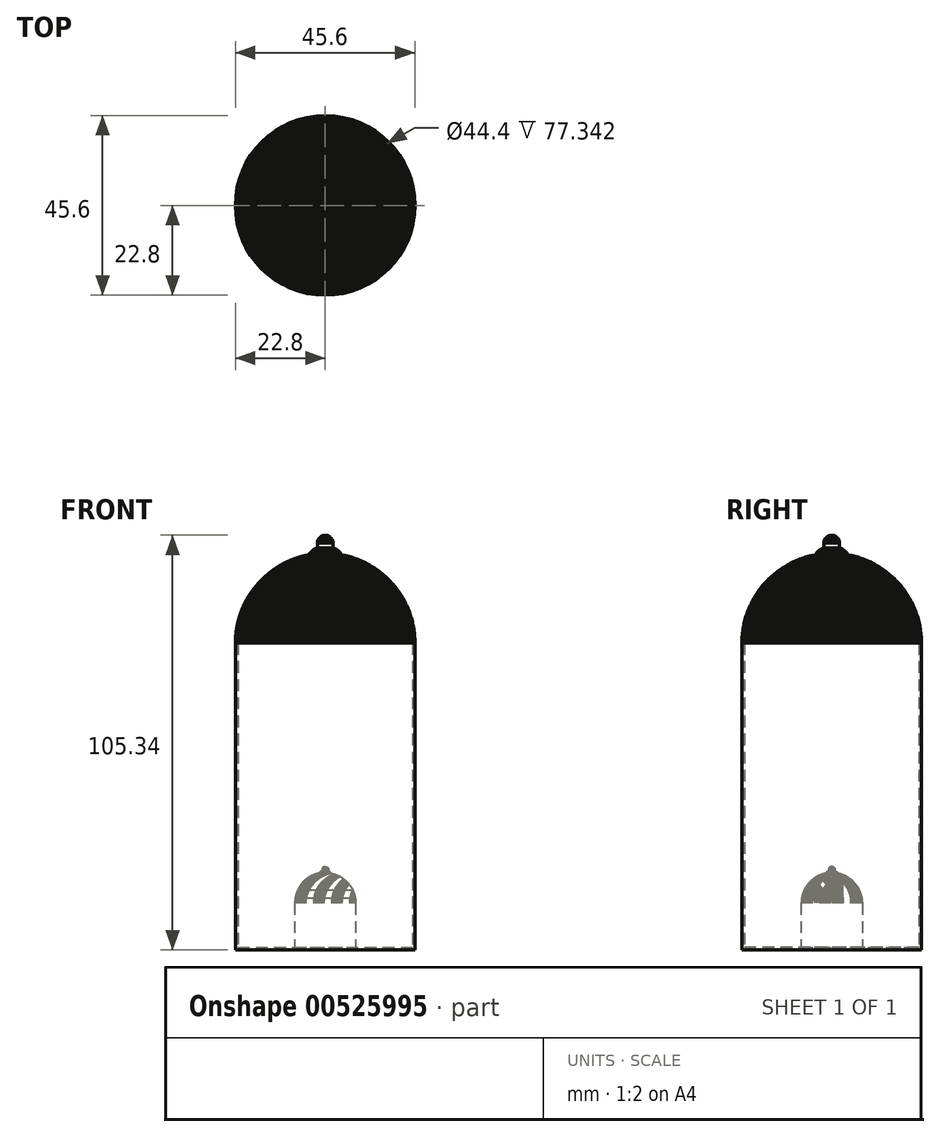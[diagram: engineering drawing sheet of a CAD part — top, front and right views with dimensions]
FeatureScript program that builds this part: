
annotation { "Feature Type Name" : "Feature", "Feature Type Description" : "" }
export const myFeature = defineFeature(function(context is Context, id is Id, definition is map)
    precondition{}
    {
        {
            var Q0;
            Q0=qCreatedBy(makeId("Front.planeOp"),FACE);
            var sketch = newSketch(context, id + "F0", { "sketchPlane" : qUnion([Q0])});
            skLineSegment(sketch, "E0", {"start": v(11.35, 52.66) * mm, "end": v(11.3, 52.66) * mm});
            skLineSegment(sketch, "E1", {"start": v(11.3, 52.66) * mm, "end": v(11.25, 52.66) * mm});
            skLineSegment(sketch, "E2", {"start": v(11.25, 52.66) * mm, "end": v(11.2, 52.66) * mm});
            skLineSegment(sketch, "E3", {"start": v(11.2, 52.66) * mm, "end": v(11.15, 52.65) * mm});
            skLineSegment(sketch, "E4", {"start": v(11.15, 52.65) * mm, "end": v(11.1, 52.64) * mm});
            skLineSegment(sketch, "E5", {"start": v(11.1, 52.64) * mm, "end": v(11.05, 52.63) * mm});
            skLineSegment(sketch, "E6", {"start": v(11.05, 52.63) * mm, "end": v(11, 52.62) * mm});
            skLineSegment(sketch, "E7", {"start": v(11, 52.62) * mm, "end": v(10.95, 52.61) * mm});
            skLineSegment(sketch, "E8", {"start": v(10.95, 52.61) * mm, "end": v(10.9, 52.6) * mm});
            skLineSegment(sketch, "E9", {"start": v(10.9, 52.6) * mm, "end": v(10.85, 52.59) * mm});
            skLineSegment(sketch, "E10", {"start": v(10.85, 52.59) * mm, "end": v(10.8, 52.58) * mm});
            skLineSegment(sketch, "E11", {"start": v(10.8, 52.58) * mm, "end": v(10.76, 52.56) * mm});
            skLineSegment(sketch, "E12", {"start": v(10.76, 52.56) * mm, "end": v(10.71, 52.54) * mm});
            skLineSegment(sketch, "E13", {"start": v(10.71, 52.54) * mm, "end": v(10.67, 52.53) * mm});
            skLineSegment(sketch, "E14", {"start": v(10.67, 52.53) * mm, "end": v(10.62, 52.5) * mm});
            skLineSegment(sketch, "E15", {"start": v(10.62, 52.5) * mm, "end": v(10.58, 52.49) * mm});
            skLineSegment(sketch, "E16", {"start": v(10.58, 52.49) * mm, "end": v(10.54, 52.47) * mm});
            skLineSegment(sketch, "E17", {"start": v(10.54, 52.47) * mm, "end": v(10.5, 52.45) * mm});
            skLineSegment(sketch, "E18", {"start": v(10.5, 52.45) * mm, "end": v(10.45, 52.42) * mm});
            skLineSegment(sketch, "E19", {"start": v(10.45, 52.42) * mm, "end": v(10.4, 52.4) * mm});
            skLineSegment(sketch, "E20", {"start": v(10.4, 52.4) * mm, "end": v(10.37, 52.38) * mm});
            skLineSegment(sketch, "E21", {"start": v(10.37, 52.38) * mm, "end": v(10.32, 52.35) * mm});
            skLineSegment(sketch, "E22", {"start": v(10.32, 52.35) * mm, "end": v(10.28, 52.32) * mm});
            skLineSegment(sketch, "E23", {"start": v(10.28, 52.32) * mm, "end": v(10.25, 52.3) * mm});
            skLineSegment(sketch, "E24", {"start": v(10.25, 52.3) * mm, "end": v(10.2, 52.27) * mm});
            skLineSegment(sketch, "E25", {"start": v(10.2, 52.27) * mm, "end": v(10.17, 52.24) * mm});
            skLineSegment(sketch, "E26", {"start": v(10.17, 52.24) * mm, "end": v(10.13, 52.2) * mm});
            skLineSegment(sketch, "E27", {"start": v(10.13, 52.2) * mm, "end": v(10.1, 52.18) * mm});
            skLineSegment(sketch, "E28", {"start": v(10.1, 52.18) * mm, "end": v(10.06, 52.15) * mm});
            skLineSegment(sketch, "E29", {"start": v(10.06, 52.15) * mm, "end": v(10.02, 52.11) * mm});
            skLineSegment(sketch, "E30", {"start": v(10.02, 52.11) * mm, "end": v(9.99, 52.08) * mm});
            skLineSegment(sketch, "E31", {"start": v(9.99, 52.08) * mm, "end": v(9.96, 52.05) * mm});
            skLineSegment(sketch, "E32", {"start": v(9.96, 52.05) * mm, "end": v(9.92, 52.01) * mm});
            skLineSegment(sketch, "E33", {"start": v(9.92, 52.01) * mm, "end": v(9.9, 51.97) * mm});
            skLineSegment(sketch, "E34", {"start": v(9.9, 51.97) * mm, "end": v(9.86, 51.94) * mm});
            skLineSegment(sketch, "E35", {"start": v(9.86, 51.94) * mm, "end": v(9.83, 51.9) * mm});
            skLineSegment(sketch, "E36", {"start": v(9.83, 51.9) * mm, "end": v(9.8, 51.86) * mm});
            skLineSegment(sketch, "E37", {"start": v(9.8, 51.86) * mm, "end": v(9.77, 51.82) * mm});
            skLineSegment(sketch, "E38", {"start": v(9.77, 51.82) * mm, "end": v(9.74, 51.78) * mm});
            skLineSegment(sketch, "E39", {"start": v(9.74, 51.78) * mm, "end": v(9.72, 51.74) * mm});
            skLineSegment(sketch, "E40", {"start": v(9.72, 51.74) * mm, "end": v(9.7, 51.7) * mm});
            skLineSegment(sketch, "E41", {"start": v(9.7, 51.7) * mm, "end": v(9.67, 51.66) * mm});
            skLineSegment(sketch, "E42", {"start": v(9.67, 51.66) * mm, "end": v(9.64, 51.62) * mm});
            skLineSegment(sketch, "E43", {"start": v(9.64, 51.62) * mm, "end": v(9.62, 51.58) * mm});
            skLineSegment(sketch, "E44", {"start": v(9.62, 51.58) * mm, "end": v(9.6, 51.53) * mm});
            skLineSegment(sketch, "E45", {"start": v(9.6, 51.53) * mm, "end": v(9.58, 51.49) * mm});
            skLineSegment(sketch, "E46", {"start": v(9.58, 51.49) * mm, "end": v(9.56, 51.45) * mm});
            skLineSegment(sketch, "E47", {"start": v(9.56, 51.45) * mm, "end": v(9.54, 51.4) * mm});
            skLineSegment(sketch, "E48", {"start": v(9.54, 51.4) * mm, "end": v(9.52, 51.35) * mm});
            skLineSegment(sketch, "E49", {"start": v(9.52, 51.35) * mm, "end": v(9.5, 51.3) * mm});
            skLineSegment(sketch, "E50", {"start": v(9.5, 51.3) * mm, "end": v(9.5, 51.26) * mm});
            skLineSegment(sketch, "E51", {"start": v(9.5, 51.26) * mm, "end": v(9.48, 51.21) * mm});
            skLineSegment(sketch, "E52", {"start": v(9.48, 51.21) * mm, "end": v(9.47, 51.17) * mm});
            skLineSegment(sketch, "E53", {"start": v(9.47, 51.17) * mm, "end": v(9.45, 51.12) * mm});
            skLineSegment(sketch, "E54", {"start": v(9.45, 51.12) * mm, "end": v(9.44, 51.07) * mm});
            skLineSegment(sketch, "E55", {"start": v(9.44, 51.07) * mm, "end": v(9.43, 51.02) * mm});
            skLineSegment(sketch, "E56", {"start": v(9.43, 51.02) * mm, "end": v(9.43, 50.97) * mm});
            skLineSegment(sketch, "E57", {"start": v(9.43, 50.97) * mm, "end": v(9.42, 50.92) * mm});
            skLineSegment(sketch, "E58", {"start": v(9.42, 50.92) * mm, "end": v(9.41, 50.87) * mm});
            skLineSegment(sketch, "E59", {"start": v(9.41, 50.87) * mm, "end": v(9.4, 50.82) * mm});
            skLineSegment(sketch, "E60", {"start": v(9.4, 50.82) * mm, "end": v(9.4, 50.77) * mm});
            skLineSegment(sketch, "E61", {"start": v(9.4, 50.77) * mm, "end": v(9.4, 50.72) * mm});
            skLineSegment(sketch, "E62", {"start": v(9.4, 50.72) * mm, "end": v(9.4, 50.67) * mm});
            skLineSegment(sketch, "E63", {"start": v(9.4, 50.67) * mm, "end": v(9.4, 50.65) * mm});
            skLineSegment(sketch, "E64", {"start": v(9.4, 50.65) * mm, "end": v(9.4, 50.63) * mm});
            skLineSegment(sketch, "E65", {"start": v(9.4, 50.63) * mm, "end": v(9.4, 50.61) * mm});
            skLineSegment(sketch, "E66", {"start": v(9.4, 50.61) * mm, "end": v(9.4, 50.6) * mm});
            skLineSegment(sketch, "E67", {"start": v(9.4, 50.6) * mm, "end": v(9.4, 50.58) * mm});
            skLineSegment(sketch, "E68", {"start": v(9.4, 50.58) * mm, "end": v(9.4, 50.56) * mm});
            skLineSegment(sketch, "E69", {"start": v(9.4, 50.56) * mm, "end": v(9.4, 50.54) * mm});
            skLineSegment(sketch, "E70", {"start": v(9.4, 50.54) * mm, "end": v(9.4, 50.52) * mm});
            skLineSegment(sketch, "E71", {"start": v(9.4, 50.52) * mm, "end": v(9.4, 50.5) * mm});
            skLineSegment(sketch, "E72", {"start": v(9.4, 50.5) * mm, "end": v(9.4, 50.49) * mm});
            skLineSegment(sketch, "E73", {"start": v(9.4, 50.49) * mm, "end": v(9.4, 50.47) * mm});
            skLineSegment(sketch, "E74", {"start": v(9.4, 50.47) * mm, "end": v(9.4, 50.45) * mm});
            skLineSegment(sketch, "E75", {"start": v(9.4, 50.45) * mm, "end": v(9.4, 50.43) * mm});
            skLineSegment(sketch, "E76", {"start": v(9.4, 50.43) * mm, "end": v(9.4, 50.41) * mm});
            skLineSegment(sketch, "E77", {"start": v(9.4, 50.41) * mm, "end": v(9.4, 50.4) * mm});
            skLineSegment(sketch, "E78", {"start": v(9.4, 50.4) * mm, "end": v(9.4, 50.37) * mm});
            skLineSegment(sketch, "E79", {"start": v(9.4, 50.37) * mm, "end": v(9.4, 50.36) * mm});
            skLineSegment(sketch, "E80", {"start": v(9.4, 50.36) * mm, "end": v(9.4, 50.34) * mm});
            skLineSegment(sketch, "E81", {"start": v(9.4, 50.34) * mm, "end": v(9.4, 50.32) * mm});
            skLineSegment(sketch, "E82", {"start": v(9.4, 50.32) * mm, "end": v(9.4, 50.3) * mm});
            skLineSegment(sketch, "E83", {"start": v(9.4, 50.3) * mm, "end": v(9.4, 50.28) * mm});
            skLineSegment(sketch, "E84", {"start": v(9.4, 50.28) * mm, "end": v(9.4, 50.26) * mm});
            skLineSegment(sketch, "E85", {"start": v(9.4, 50.26) * mm, "end": v(9.4, 50.25) * mm});
            skLineSegment(sketch, "E86", {"start": v(9.4, 50.25) * mm, "end": v(9.4, 50.23) * mm});
            skLineSegment(sketch, "E87", {"start": v(9.4, 50.23) * mm, "end": v(9.4, 50.2) * mm});
            skLineSegment(sketch, "E88", {"start": v(9.4, 50.2) * mm, "end": v(9.4, 50.2) * mm});
            skLineSegment(sketch, "E89", {"start": v(9.4, 50.2) * mm, "end": v(9.4, 50.17) * mm});
            skLineSegment(sketch, "E90", {"start": v(9.4, 50.17) * mm, "end": v(9.4, 50.15) * mm});
            skLineSegment(sketch, "E91", {"start": v(9.4, 50.15) * mm, "end": v(9.4, 50.14) * mm});
            skLineSegment(sketch, "E92", {"start": v(9.4, 50.14) * mm, "end": v(9.4, 50.12) * mm});
            skLineSegment(sketch, "E93", {"start": v(9.4, 50.12) * mm, "end": v(9.4, 50.1) * mm});
            skLineSegment(sketch, "E94", {"start": v(9.4, 50.1) * mm, "end": v(9.4, 50.08) * mm});
            skLineSegment(sketch, "E95", {"start": v(9.4, 50.08) * mm, "end": v(9.4, 50.06) * mm});
            skLineSegment(sketch, "E96", {"start": v(9.4, 50.06) * mm, "end": v(9.4, 50.04) * mm});
            skLineSegment(sketch, "E97", {"start": v(9.4, 50.04) * mm, "end": v(9.4, 50.03) * mm});
            skLineSegment(sketch, "E98", {"start": v(9.4, 50.03) * mm, "end": v(9.4, 50) * mm});
            skLineSegment(sketch, "E99", {"start": v(9.4, 50) * mm, "end": v(9.4, 49.99) * mm});
            skLineSegment(sketch, "E100", {"start": v(9.4, 49.99) * mm, "end": v(9.4, 49.97) * mm});
            skLineSegment(sketch, "E101", {"start": v(9.4, 49.97) * mm, "end": v(9.4, 49.95) * mm});
            skLineSegment(sketch, "E102", {"start": v(9.4, 49.95) * mm, "end": v(9.4, 49.93) * mm});
            skLineSegment(sketch, "E103", {"start": v(9.4, 49.93) * mm, "end": v(9.4, 49.92) * mm});
            skLineSegment(sketch, "E104", {"start": v(9.4, 49.92) * mm, "end": v(9.4, 49.9) * mm});
            skLineSegment(sketch, "E105", {"start": v(9.4, 49.9) * mm, "end": v(9.4, 49.88) * mm});
            skLineSegment(sketch, "E106", {"start": v(9.4, 49.88) * mm, "end": v(9.4, 49.86) * mm});
            skLineSegment(sketch, "E107", {"start": v(9.4, 49.86) * mm, "end": v(9.4, 49.84) * mm});
            skLineSegment(sketch, "E108", {"start": v(9.4, 49.84) * mm, "end": v(9.4, 49.82) * mm});
            skLineSegment(sketch, "E109", {"start": v(9.4, 49.82) * mm, "end": v(9.4, 49.8) * mm});
            skLineSegment(sketch, "E110", {"start": v(9.4, 49.8) * mm, "end": v(9.4, 49.79) * mm});
            skLineSegment(sketch, "E111", {"start": v(9.4, 49.79) * mm, "end": v(9.4, 49.77) * mm});
            skLineSegment(sketch, "E112", {"start": v(9.4, 49.77) * mm, "end": v(9.4, 49.75) * mm});
            skLineSegment(sketch, "E113", {"start": v(9.4, 49.75) * mm, "end": v(9.4, 49.73) * mm});
            skLineSegment(sketch, "E114", {"start": v(9.4, 49.73) * mm, "end": v(9.4, 49.71) * mm});
            skLineSegment(sketch, "E115", {"start": v(9.4, 49.71) * mm, "end": v(9.4, 49.7) * mm});
            skLineSegment(sketch, "E116", {"start": v(9.4, 49.7) * mm, "end": v(9.4, 49.68) * mm});
            skLineSegment(sketch, "E117", {"start": v(9.4, 49.68) * mm, "end": v(9.4, 49.66) * mm});
            skLineSegment(sketch, "E118", {"start": v(9.4, 49.66) * mm, "end": v(9.4, 49.64) * mm});
            skLineSegment(sketch, "E119", {"start": v(9.4, 49.64) * mm, "end": v(9.4, 49.62) * mm});
            skLineSegment(sketch, "E120", {"start": v(9.4, 49.62) * mm, "end": v(9.4, 49.6) * mm});
            skLineSegment(sketch, "E121", {"start": v(9.4, 49.6) * mm, "end": v(9.4, 49.58) * mm});
            skLineSegment(sketch, "E122", {"start": v(9.4, 49.58) * mm, "end": v(9.4, 49.57) * mm});
            skLineSegment(sketch, "E123", {"start": v(9.4, 49.57) * mm, "end": v(9.4, 49.55) * mm});
            skLineSegment(sketch, "E124", {"start": v(9.4, 49.55) * mm, "end": v(9.4, 49.53) * mm});
            skLineSegment(sketch, "E125", {"start": v(9.4, 49.53) * mm, "end": v(9.4, 49.51) * mm});
            skLineSegment(sketch, "E126", {"start": v(9.4, 49.51) * mm, "end": v(9.4, 49.5) * mm});
            skLineSegment(sketch, "E127", {"start": v(9.4, 49.5) * mm, "end": v(9.36, 49.47) * mm});
            skLineSegment(sketch, "E128", {"start": v(9.36, 49.47) * mm, "end": v(9.3, 49.46) * mm});
            skLineSegment(sketch, "E129", {"start": v(9.3, 49.46) * mm, "end": v(9.26, 49.44) * mm});
            skLineSegment(sketch, "E130", {"start": v(9.26, 49.44) * mm, "end": v(9.22, 49.42) * mm});
            skLineSegment(sketch, "E131", {"start": v(9.22, 49.42) * mm, "end": v(9.17, 49.4) * mm});
            skLineSegment(sketch, "E132", {"start": v(9.17, 49.4) * mm, "end": v(9.13, 49.38) * mm});
            skLineSegment(sketch, "E133", {"start": v(9.13, 49.38) * mm, "end": v(9.08, 49.36) * mm});
            skLineSegment(sketch, "E134", {"start": v(9.08, 49.36) * mm, "end": v(9.04, 49.34) * mm});
            skLineSegment(sketch, "E135", {"start": v(9.04, 49.34) * mm, "end": v(9, 49.32) * mm});
            skLineSegment(sketch, "E136", {"start": v(9, 49.32) * mm, "end": v(8.95, 49.3) * mm});
            skLineSegment(sketch, "E137", {"start": v(8.95, 49.3) * mm, "end": v(8.9, 49.28) * mm});
            skLineSegment(sketch, "E138", {"start": v(8.9, 49.28) * mm, "end": v(8.86, 49.25) * mm});
            skLineSegment(sketch, "E139", {"start": v(8.86, 49.25) * mm, "end": v(8.82, 49.23) * mm});
            skLineSegment(sketch, "E140", {"start": v(8.82, 49.23) * mm, "end": v(8.77, 49.2) * mm});
            skLineSegment(sketch, "E141", {"start": v(8.77, 49.2) * mm, "end": v(8.73, 49.19) * mm});
            skLineSegment(sketch, "E142", {"start": v(8.73, 49.19) * mm, "end": v(8.7, 49.16) * mm});
            skLineSegment(sketch, "E143", {"start": v(8.7, 49.16) * mm, "end": v(8.65, 49.14) * mm});
            skLineSegment(sketch, "E144", {"start": v(8.65, 49.14) * mm, "end": v(8.6, 49.11) * mm});
            skLineSegment(sketch, "E145", {"start": v(8.6, 49.11) * mm, "end": v(8.57, 49.1) * mm});
            skLineSegment(sketch, "E146", {"start": v(8.57, 49.1) * mm, "end": v(8.53, 49.07) * mm});
            skLineSegment(sketch, "E147", {"start": v(8.53, 49.07) * mm, "end": v(8.49, 49.04) * mm});
            skLineSegment(sketch, "E148", {"start": v(8.49, 49.04) * mm, "end": v(8.45, 49.01) * mm});
            skLineSegment(sketch, "E149", {"start": v(8.45, 49.01) * mm, "end": v(8.4, 48.99) * mm});
            skLineSegment(sketch, "E150", {"start": v(8.4, 48.99) * mm, "end": v(8.37, 48.96) * mm});
            skLineSegment(sketch, "E151", {"start": v(8.37, 48.96) * mm, "end": v(8.33, 48.94) * mm});
            skLineSegment(sketch, "E152", {"start": v(8.33, 48.94) * mm, "end": v(8.3, 48.91) * mm});
            skLineSegment(sketch, "E153", {"start": v(8.3, 48.91) * mm, "end": v(8.26, 48.88) * mm});
            skLineSegment(sketch, "E154", {"start": v(8.26, 48.88) * mm, "end": v(8.22, 48.86) * mm});
            skLineSegment(sketch, "E155", {"start": v(8.22, 48.86) * mm, "end": v(8.18, 48.83) * mm});
            skLineSegment(sketch, "E156", {"start": v(8.18, 48.83) * mm, "end": v(8.15, 48.8) * mm});
            skLineSegment(sketch, "E157", {"start": v(8.15, 48.8) * mm, "end": v(8.11, 48.77) * mm});
            skLineSegment(sketch, "E158", {"start": v(8.11, 48.77) * mm, "end": v(8.08, 48.74) * mm});
            skLineSegment(sketch, "E159", {"start": v(8.08, 48.74) * mm, "end": v(8.04, 48.71) * mm});
            skLineSegment(sketch, "E160", {"start": v(8.04, 48.71) * mm, "end": v(8, 48.69) * mm});
            skLineSegment(sketch, "E161", {"start": v(8, 48.69) * mm, "end": v(7.98, 48.66) * mm});
            skLineSegment(sketch, "E162", {"start": v(7.98, 48.66) * mm, "end": v(7.94, 48.63) * mm});
            skLineSegment(sketch, "E163", {"start": v(7.94, 48.63) * mm, "end": v(7.91, 48.6) * mm});
            skLineSegment(sketch, "E164", {"start": v(7.91, 48.6) * mm, "end": v(7.88, 48.57) * mm});
            skLineSegment(sketch, "E165", {"start": v(7.88, 48.57) * mm, "end": v(7.85, 48.53) * mm});
            skLineSegment(sketch, "E166", {"start": v(7.85, 48.53) * mm, "end": v(7.82, 48.5) * mm});
            skLineSegment(sketch, "E167", {"start": v(7.82, 48.5) * mm, "end": v(7.78, 48.47) * mm});
            skLineSegment(sketch, "E168", {"start": v(7.78, 48.47) * mm, "end": v(7.75, 48.44) * mm});
            skLineSegment(sketch, "E169", {"start": v(7.75, 48.44) * mm, "end": v(7.72, 48.4) * mm});
            skLineSegment(sketch, "E170", {"start": v(7.72, 48.4) * mm, "end": v(7.7, 48.38) * mm});
            skLineSegment(sketch, "E171", {"start": v(7.7, 48.38) * mm, "end": v(7.67, 48.35) * mm});
            skLineSegment(sketch, "E172", {"start": v(7.67, 48.35) * mm, "end": v(7.64, 48.31) * mm});
            skLineSegment(sketch, "E173", {"start": v(7.64, 48.31) * mm, "end": v(7.61, 48.28) * mm});
            skLineSegment(sketch, "E174", {"start": v(7.61, 48.28) * mm, "end": v(7.58, 48.25) * mm});
            skLineSegment(sketch, "E175", {"start": v(7.58, 48.25) * mm, "end": v(7.56, 48.21) * mm});
            skLineSegment(sketch, "E176", {"start": v(7.56, 48.21) * mm, "end": v(7.53, 48.18) * mm});
            skLineSegment(sketch, "E177", {"start": v(7.53, 48.18) * mm, "end": v(7.5, 48.15) * mm});
            skLineSegment(sketch, "E178", {"start": v(7.5, 48.15) * mm, "end": v(7.48, 48.11) * mm});
            skLineSegment(sketch, "E179", {"start": v(7.48, 48.11) * mm, "end": v(7.45, 48.08) * mm});
            skLineSegment(sketch, "E180", {"start": v(7.45, 48.08) * mm, "end": v(7.43, 48.04) * mm});
            skLineSegment(sketch, "E181", {"start": v(7.43, 48.04) * mm, "end": v(7.4, 48) * mm});
            skLineSegment(sketch, "E182", {"start": v(7.4, 48) * mm, "end": v(7.38, 47.97) * mm});
            skLineSegment(sketch, "E183", {"start": v(7.38, 47.97) * mm, "end": v(7.36, 47.94) * mm});
            skLineSegment(sketch, "E184", {"start": v(7.36, 47.94) * mm, "end": v(7.34, 47.9) * mm});
            skLineSegment(sketch, "E185", {"start": v(7.34, 47.9) * mm, "end": v(7.32, 47.87) * mm});
            skLineSegment(sketch, "E186", {"start": v(7.32, 47.87) * mm, "end": v(7.3, 47.83) * mm});
            skLineSegment(sketch, "E187", {"start": v(7.3, 47.83) * mm, "end": v(7.28, 47.8) * mm});
            skLineSegment(sketch, "E188", {"start": v(7.28, 47.8) * mm, "end": v(7.26, 47.76) * mm});
            skLineSegment(sketch, "E189", {"start": v(7.26, 47.76) * mm, "end": v(7.24, 47.72) * mm});
            skLineSegment(sketch, "E190", {"start": v(7.24, 47.72) * mm, "end": v(7.22, 47.69) * mm});
            skLineSegment(sketch, "E191", {"start": v(7.22, 47.69) * mm, "end": v(6.71, 47.59) * mm});
            skLineSegment(sketch, "E192", {"start": v(6.71, 47.59) * mm, "end": v(6.21, 47.48) * mm});
            skLineSegment(sketch, "E193", {"start": v(6.21, 47.48) * mm, "end": v(5.72, 47.36) * mm});
            skLineSegment(sketch, "E194", {"start": v(5.72, 47.36) * mm, "end": v(5.23, 47.23) * mm});
            skLineSegment(sketch, "E195", {"start": v(5.23, 47.23) * mm, "end": v(4.74, 47.08) * mm});
            skLineSegment(sketch, "E196", {"start": v(4.74, 47.08) * mm, "end": v(4.26, 46.93) * mm});
            skLineSegment(sketch, "E197", {"start": v(4.26, 46.93) * mm, "end": v(3.79, 46.77) * mm});
            skLineSegment(sketch, "E198", {"start": v(3.79, 46.77) * mm, "end": v(3.32, 46.6) * mm});
            skLineSegment(sketch, "E199", {"start": v(3.32, 46.6) * mm, "end": v(2.85, 46.42) * mm});
            skLineSegment(sketch, "E200", {"start": v(2.85, 46.42) * mm, "end": v(2.4, 46.23) * mm});
            skLineSegment(sketch, "E201", {"start": v(2.4, 46.23) * mm, "end": v(1.94, 46.03) * mm});
            skLineSegment(sketch, "E202", {"start": v(1.94, 46.03) * mm, "end": v(1.5, 45.82) * mm});
            skLineSegment(sketch, "E203", {"start": v(1.5, 45.82) * mm, "end": v(1.05, 45.6) * mm});
            skLineSegment(sketch, "E204", {"start": v(1.05, 45.6) * mm, "end": v(0.61, 45.37) * mm});
            skLineSegment(sketch, "E205", {"start": v(0.61, 45.37) * mm, "end": v(0.18, 45.13) * mm});
            skLineSegment(sketch, "E206", {"start": v(0.18, 45.13) * mm, "end": v(-0.25, 44.89) * mm});
            skLineSegment(sketch, "E207", {"start": v(-0.25, 44.89) * mm, "end": v(-0.67, 44.63) * mm});
            skLineSegment(sketch, "E208", {"start": v(-0.67, 44.63) * mm, "end": v(-1.08, 44.37) * mm});
            skLineSegment(sketch, "E209", {"start": v(-1.08, 44.37) * mm, "end": v(-1.48, 44.1) * mm});
            skLineSegment(sketch, "E210", {"start": v(-1.48, 44.1) * mm, "end": v(-1.88, 43.82) * mm});
            skLineSegment(sketch, "E211", {"start": v(-1.88, 43.82) * mm, "end": v(-2.28, 43.53) * mm});
            skLineSegment(sketch, "E212", {"start": v(-2.28, 43.53) * mm, "end": v(-2.67, 43.24) * mm});
            skLineSegment(sketch, "E213", {"start": v(-2.67, 43.24) * mm, "end": v(-3.04, 42.93) * mm});
            skLineSegment(sketch, "E214", {"start": v(-3.04, 42.93) * mm, "end": v(-3.42, 42.62) * mm});
            skLineSegment(sketch, "E215", {"start": v(-3.42, 42.62) * mm, "end": v(-3.78, 42.3) * mm});
            skLineSegment(sketch, "E216", {"start": v(-3.78, 42.3) * mm, "end": v(-4.14, 41.97) * mm});
            skLineSegment(sketch, "E217", {"start": v(-4.14, 41.97) * mm, "end": v(-4.5, 41.64) * mm});
            skLineSegment(sketch, "E218", {"start": v(-4.5, 41.64) * mm, "end": v(-4.84, 41.3) * mm});
            skLineSegment(sketch, "E219", {"start": v(-4.84, 41.3) * mm, "end": v(-5.18, 40.95) * mm});
            skLineSegment(sketch, "E220", {"start": v(-5.18, 40.95) * mm, "end": v(-5.5, 40.6) * mm});
            skLineSegment(sketch, "E221", {"start": v(-5.5, 40.6) * mm, "end": v(-5.83, 40.23) * mm});
            skLineSegment(sketch, "E222", {"start": v(-5.83, 40.23) * mm, "end": v(-6.14, 39.86) * mm});
            skLineSegment(sketch, "E223", {"start": v(-6.14, 39.86) * mm, "end": v(-6.45, 39.48) * mm});
            skLineSegment(sketch, "E224", {"start": v(-6.45, 39.48) * mm, "end": v(-6.74, 39.1) * mm});
            skLineSegment(sketch, "E225", {"start": v(-6.74, 39.1) * mm, "end": v(-7.03, 38.71) * mm});
            skLineSegment(sketch, "E226", {"start": v(-7.03, 38.71) * mm, "end": v(-7.31, 38.32) * mm});
            skLineSegment(sketch, "E227", {"start": v(-7.31, 38.32) * mm, "end": v(-7.59, 37.92) * mm});
            skLineSegment(sketch, "E228", {"start": v(-7.59, 37.92) * mm, "end": v(-7.85, 37.5) * mm});
            skLineSegment(sketch, "E229", {"start": v(-7.85, 37.5) * mm, "end": v(-8.1, 37.1) * mm});
            skLineSegment(sketch, "E230", {"start": v(-8.1, 37.1) * mm, "end": v(-8.36, 36.68) * mm});
            skLineSegment(sketch, "E231", {"start": v(-8.36, 36.68) * mm, "end": v(-8.6, 36.25) * mm});
            skLineSegment(sketch, "E232", {"start": v(-8.6, 36.25) * mm, "end": v(-8.82, 35.82) * mm});
            skLineSegment(sketch, "E233", {"start": v(-8.82, 35.82) * mm, "end": v(-9.05, 35.39) * mm});
            skLineSegment(sketch, "E234", {"start": v(-9.05, 35.39) * mm, "end": v(-9.26, 34.95) * mm});
            skLineSegment(sketch, "E235", {"start": v(-9.26, 34.95) * mm, "end": v(-9.46, 34.5) * mm});
            skLineSegment(sketch, "E236", {"start": v(-9.46, 34.5) * mm, "end": v(-9.65, 34.05) * mm});
            skLineSegment(sketch, "E237", {"start": v(-9.65, 34.05) * mm, "end": v(-9.84, 33.6) * mm});
            skLineSegment(sketch, "E238", {"start": v(-9.84, 33.6) * mm, "end": v(-10, 33.14) * mm});
            skLineSegment(sketch, "E239", {"start": v(-10, 33.14) * mm, "end": v(-10.17, 32.68) * mm});
            skLineSegment(sketch, "E240", {"start": v(-10.17, 32.68) * mm, "end": v(-10.33, 32.2) * mm});
            skLineSegment(sketch, "E241", {"start": v(-10.33, 32.2) * mm, "end": v(-10.47, 31.74) * mm});
            skLineSegment(sketch, "E242", {"start": v(-10.47, 31.74) * mm, "end": v(-10.6, 31.26) * mm});
            skLineSegment(sketch, "E243", {"start": v(-10.6, 31.26) * mm, "end": v(-10.73, 30.78) * mm});
            skLineSegment(sketch, "E244", {"start": v(-10.73, 30.78) * mm, "end": v(-10.85, 30.3) * mm});
            skLineSegment(sketch, "E245", {"start": v(-10.85, 30.3) * mm, "end": v(-10.95, 29.8) * mm});
            skLineSegment(sketch, "E246", {"start": v(-10.95, 29.8) * mm, "end": v(-11.04, 29.32) * mm});
            skLineSegment(sketch, "E247", {"start": v(-11.04, 29.32) * mm, "end": v(-11.13, 28.82) * mm});
            skLineSegment(sketch, "E248", {"start": v(-11.13, 28.82) * mm, "end": v(-11.2, 28.33) * mm});
            skLineSegment(sketch, "E249", {"start": v(-11.2, 28.33) * mm, "end": v(-11.26, 27.82) * mm});
            skLineSegment(sketch, "E250", {"start": v(-11.26, 27.82) * mm, "end": v(-11.3, 27.32) * mm});
            skLineSegment(sketch, "E251", {"start": v(-11.3, 27.32) * mm, "end": v(-11.35, 26.81) * mm});
            skLineSegment(sketch, "E252", {"start": v(-11.35, 26.81) * mm, "end": v(-11.38, 26.3) * mm});
            skLineSegment(sketch, "E253", {"start": v(-11.38, 26.3) * mm, "end": v(-11.4, 25.8) * mm});
            skLineSegment(sketch, "E254", {"start": v(-11.4, 25.8) * mm, "end": v(-11.4, 25.28) * mm});
            skLineSegment(sketch, "E255", {"start": v(-11.4, 25.28) * mm, "end": v(-11.4, 24.06) * mm});
            skLineSegment(sketch, "E256", {"start": v(-11.4, 24.06) * mm, "end": v(-11.4, 22.84) * mm});
            skLineSegment(sketch, "E257", {"start": v(-11.4, 22.84) * mm, "end": v(-11.4, 21.62) * mm});
            skLineSegment(sketch, "E258", {"start": v(-11.4, 21.62) * mm, "end": v(-11.4, 20.4) * mm});
            skLineSegment(sketch, "E259", {"start": v(-11.4, 20.4) * mm, "end": v(-11.4, 19.19) * mm});
            skLineSegment(sketch, "E260", {"start": v(-11.4, 19.19) * mm, "end": v(-11.4, 17.97) * mm});
            skLineSegment(sketch, "E261", {"start": v(-11.4, 17.97) * mm, "end": v(-11.4, 16.75) * mm});
            skLineSegment(sketch, "E262", {"start": v(-11.4, 16.75) * mm, "end": v(-11.4, 15.53) * mm});
            skLineSegment(sketch, "E263", {"start": v(-11.4, 15.53) * mm, "end": v(-11.4, 14.32) * mm});
            skLineSegment(sketch, "E264", {"start": v(-11.4, 14.32) * mm, "end": v(-11.4, 13.1) * mm});
            skLineSegment(sketch, "E265", {"start": v(-11.4, 13.1) * mm, "end": v(-11.4, 11.88) * mm});
            skLineSegment(sketch, "E266", {"start": v(-11.4, 11.88) * mm, "end": v(-11.4, 10.66) * mm});
            skLineSegment(sketch, "E267", {"start": v(-11.4, 10.66) * mm, "end": v(-11.4, 9.44) * mm});
            skLineSegment(sketch, "E268", {"start": v(-11.4, 9.44) * mm, "end": v(-11.4, 8.23) * mm});
            skLineSegment(sketch, "E269", {"start": v(-11.4, 8.23) * mm, "end": v(-11.4, 7) * mm});
            skLineSegment(sketch, "E270", {"start": v(-11.4, 7) * mm, "end": v(-11.4, 5.8) * mm});
            skLineSegment(sketch, "E271", {"start": v(-11.4, 5.8) * mm, "end": v(-11.4, 4.57) * mm});
            skLineSegment(sketch, "E272", {"start": v(-11.4, 4.57) * mm, "end": v(-11.4, 3.36) * mm});
            skLineSegment(sketch, "E273", {"start": v(-11.4, 3.36) * mm, "end": v(-11.4, 2.14) * mm});
            skLineSegment(sketch, "E274", {"start": v(-11.4, 2.14) * mm, "end": v(-11.4, 0.92) * mm});
            skLineSegment(sketch, "E275", {"start": v(-11.4, 0.92) * mm, "end": v(-11.4, -0.3) * mm});
            skLineSegment(sketch, "E276", {"start": v(-11.4, -0.3) * mm, "end": v(-11.4, -1.52) * mm});
            skLineSegment(sketch, "E277", {"start": v(-11.4, -1.52) * mm, "end": v(-11.4, -2.73) * mm});
            skLineSegment(sketch, "E278", {"start": v(-11.4, -2.73) * mm, "end": v(-11.4, -3.95) * mm});
            skLineSegment(sketch, "E279", {"start": v(-11.4, -3.95) * mm, "end": v(-11.4, -5.17) * mm});
            skLineSegment(sketch, "E280", {"start": v(-11.4, -5.17) * mm, "end": v(-11.4, -6.39) * mm});
            skLineSegment(sketch, "E281", {"start": v(-11.4, -6.39) * mm, "end": v(-11.4, -7.6) * mm});
            skLineSegment(sketch, "E282", {"start": v(-11.4, -7.6) * mm, "end": v(-11.4, -8.82) * mm});
            skLineSegment(sketch, "E283", {"start": v(-11.4, -8.82) * mm, "end": v(-11.4, -10.04) * mm});
            skLineSegment(sketch, "E284", {"start": v(-11.4, -10.04) * mm, "end": v(-11.4, -11.26) * mm});
            skLineSegment(sketch, "E285", {"start": v(-11.4, -11.26) * mm, "end": v(-11.4, -12.48) * mm});
            skLineSegment(sketch, "E286", {"start": v(-11.4, -12.48) * mm, "end": v(-11.4, -13.7) * mm});
            skLineSegment(sketch, "E287", {"start": v(-11.4, -13.7) * mm, "end": v(-11.4, -14.91) * mm});
            skLineSegment(sketch, "E288", {"start": v(-11.4, -14.91) * mm, "end": v(-11.4, -16.13) * mm});
            skLineSegment(sketch, "E289", {"start": v(-11.4, -16.13) * mm, "end": v(-11.4, -17.35) * mm});
            skLineSegment(sketch, "E290", {"start": v(-11.4, -17.35) * mm, "end": v(-11.4, -18.57) * mm});
            skLineSegment(sketch, "E291", {"start": v(-11.4, -18.57) * mm, "end": v(-11.4, -19.78) * mm});
            skLineSegment(sketch, "E292", {"start": v(-11.4, -19.78) * mm, "end": v(-11.4, -21) * mm});
            skLineSegment(sketch, "E293", {"start": v(-11.4, -21) * mm, "end": v(-11.4, -22.22) * mm});
            skLineSegment(sketch, "E294", {"start": v(-11.4, -22.22) * mm, "end": v(-11.4, -23.44) * mm});
            skLineSegment(sketch, "E295", {"start": v(-11.4, -23.44) * mm, "end": v(-11.4, -24.66) * mm});
            skLineSegment(sketch, "E296", {"start": v(-11.4, -24.66) * mm, "end": v(-11.4, -25.87) * mm});
            skLineSegment(sketch, "E297", {"start": v(-11.4, -25.87) * mm, "end": v(-11.4, -27.1) * mm});
            skLineSegment(sketch, "E298", {"start": v(-11.4, -27.1) * mm, "end": v(-11.4, -28.3) * mm});
            skLineSegment(sketch, "E299", {"start": v(-11.4, -28.3) * mm, "end": v(-11.4, -29.53) * mm});
            skLineSegment(sketch, "E300", {"start": v(-11.4, -29.53) * mm, "end": v(-11.4, -30.74) * mm});
            skLineSegment(sketch, "E301", {"start": v(-11.4, -30.74) * mm, "end": v(-11.4, -31.96) * mm});
            skLineSegment(sketch, "E302", {"start": v(-11.4, -31.96) * mm, "end": v(-11.4, -33.18) * mm});
            skLineSegment(sketch, "E303", {"start": v(-11.4, -33.18) * mm, "end": v(-11.4, -34.4) * mm});
            skLineSegment(sketch, "E304", {"start": v(-11.4, -34.4) * mm, "end": v(-11.4, -35.62) * mm});
            skLineSegment(sketch, "E305", {"start": v(-11.4, -35.62) * mm, "end": v(-11.4, -36.83) * mm});
            skLineSegment(sketch, "E306", {"start": v(-11.4, -36.83) * mm, "end": v(-11.4, -38.05) * mm});
            skLineSegment(sketch, "E307", {"start": v(-11.4, -38.05) * mm, "end": v(-11.4, -39.27) * mm});
            skLineSegment(sketch, "E308", {"start": v(-11.4, -39.27) * mm, "end": v(-11.4, -40.49) * mm});
            skLineSegment(sketch, "E309", {"start": v(-11.4, -40.49) * mm, "end": v(-11.4, -41.7) * mm});
            skLineSegment(sketch, "E310", {"start": v(-11.4, -41.7) * mm, "end": v(-11.4, -42.92) * mm});
            skLineSegment(sketch, "E311", {"start": v(-11.4, -42.92) * mm, "end": v(-11.4, -44.14) * mm});
            skLineSegment(sketch, "E312", {"start": v(-11.4, -44.14) * mm, "end": v(-11.4, -45.36) * mm});
            skLineSegment(sketch, "E313", {"start": v(-11.4, -45.36) * mm, "end": v(-11.4, -46.58) * mm});
            skLineSegment(sketch, "E314", {"start": v(-11.4, -46.58) * mm, "end": v(-11.4, -47.8) * mm});
            skLineSegment(sketch, "E315", {"start": v(-11.4, -47.8) * mm, "end": v(-11.4, -49.01) * mm});
            skLineSegment(sketch, "E316", {"start": v(-11.4, -49.01) * mm, "end": v(-11.4, -50.23) * mm});
            skLineSegment(sketch, "E317", {"start": v(-11.4, -50.23) * mm, "end": v(-11.4, -51.45) * mm});
            skLineSegment(sketch, "E318", {"start": v(-11.4, -51.45) * mm, "end": v(-11.4, -52.67) * mm});
            skLineSegment(sketch, "E319", {"start": v(-11.4, -52.67) * mm, "end": v(-11.16, -52.67) * mm});
            skLineSegment(sketch, "E320", {"start": v(-11.16, -52.67) * mm, "end": v(-10.91, -52.67) * mm});
            skLineSegment(sketch, "E321", {"start": v(-10.91, -52.67) * mm, "end": v(-10.67, -52.67) * mm});
            skLineSegment(sketch, "E322", {"start": v(-10.67, -52.67) * mm, "end": v(-10.42, -52.67) * mm});
            skLineSegment(sketch, "E323", {"start": v(-10.42, -52.67) * mm, "end": v(-10.18, -52.67) * mm});
            skLineSegment(sketch, "E324", {"start": v(-10.18, -52.67) * mm, "end": v(-9.93, -52.67) * mm});
            skLineSegment(sketch, "E325", {"start": v(-9.93, -52.67) * mm, "end": v(-9.69, -52.67) * mm});
            skLineSegment(sketch, "E326", {"start": v(-9.69, -52.67) * mm, "end": v(-9.44, -52.67) * mm});
            skLineSegment(sketch, "E327", {"start": v(-9.44, -52.67) * mm, "end": v(-9.2, -52.67) * mm});
            skLineSegment(sketch, "E328", {"start": v(-9.2, -52.67) * mm, "end": v(-8.95, -52.67) * mm});
            skLineSegment(sketch, "E329", {"start": v(-8.95, -52.67) * mm, "end": v(-8.71, -52.67) * mm});
            skLineSegment(sketch, "E330", {"start": v(-8.71, -52.67) * mm, "end": v(-8.47, -52.67) * mm});
            skLineSegment(sketch, "E331", {"start": v(-8.47, -52.67) * mm, "end": v(-8.22, -52.67) * mm});
            skLineSegment(sketch, "E332", {"start": v(-8.22, -52.67) * mm, "end": v(-7.98, -52.67) * mm});
            skLineSegment(sketch, "E333", {"start": v(-7.98, -52.67) * mm, "end": v(-7.73, -52.67) * mm});
            skLineSegment(sketch, "E334", {"start": v(-7.73, -52.67) * mm, "end": v(-7.49, -52.67) * mm});
            skLineSegment(sketch, "E335", {"start": v(-7.49, -52.67) * mm, "end": v(-7.24, -52.67) * mm});
            skLineSegment(sketch, "E336", {"start": v(-7.24, -52.67) * mm, "end": v(-7, -52.67) * mm});
            skLineSegment(sketch, "E337", {"start": v(-7, -52.67) * mm, "end": v(-6.75, -52.67) * mm});
            skLineSegment(sketch, "E338", {"start": v(-6.75, -52.67) * mm, "end": v(-6.5, -52.67) * mm});
            skLineSegment(sketch, "E339", {"start": v(-6.5, -52.67) * mm, "end": v(-6.26, -52.67) * mm});
            skLineSegment(sketch, "E340", {"start": v(-6.26, -52.67) * mm, "end": v(-6.02, -52.67) * mm});
            skLineSegment(sketch, "E341", {"start": v(-6.02, -52.67) * mm, "end": v(-5.78, -52.67) * mm});
            skLineSegment(sketch, "E342", {"start": v(-5.78, -52.67) * mm, "end": v(-5.53, -52.67) * mm});
            skLineSegment(sketch, "E343", {"start": v(-5.53, -52.67) * mm, "end": v(-5.29, -52.67) * mm});
            skLineSegment(sketch, "E344", {"start": v(-5.29, -52.67) * mm, "end": v(-5.04, -52.67) * mm});
            skLineSegment(sketch, "E345", {"start": v(-5.04, -52.67) * mm, "end": v(-4.8, -52.67) * mm});
            skLineSegment(sketch, "E346", {"start": v(-4.8, -52.67) * mm, "end": v(-4.55, -52.67) * mm});
            skLineSegment(sketch, "E347", {"start": v(-4.55, -52.67) * mm, "end": v(-4.3, -52.67) * mm});
            skLineSegment(sketch, "E348", {"start": v(-4.3, -52.67) * mm, "end": v(-4.06, -52.67) * mm});
            skLineSegment(sketch, "E349", {"start": v(-4.06, -52.67) * mm, "end": v(-3.82, -52.67) * mm});
            skLineSegment(sketch, "E350", {"start": v(-3.82, -52.67) * mm, "end": v(-3.57, -52.67) * mm});
            skLineSegment(sketch, "E351", {"start": v(-3.57, -52.67) * mm, "end": v(-3.33, -52.67) * mm});
            skLineSegment(sketch, "E352", {"start": v(-3.33, -52.67) * mm, "end": v(-3.09, -52.67) * mm});
            skLineSegment(sketch, "E353", {"start": v(-3.09, -52.67) * mm, "end": v(-2.84, -52.67) * mm});
            skLineSegment(sketch, "E354", {"start": v(-2.84, -52.67) * mm, "end": v(-2.6, -52.67) * mm});
            skLineSegment(sketch, "E355", {"start": v(-2.6, -52.67) * mm, "end": v(-2.35, -52.67) * mm});
            skLineSegment(sketch, "E356", {"start": v(-2.35, -52.67) * mm, "end": v(-2.1, -52.67) * mm});
            skLineSegment(sketch, "E357", {"start": v(-2.1, -52.67) * mm, "end": v(-1.86, -52.67) * mm});
            skLineSegment(sketch, "E358", {"start": v(-1.86, -52.67) * mm, "end": v(-1.62, -52.67) * mm});
            skLineSegment(sketch, "E359", {"start": v(-1.62, -52.67) * mm, "end": v(-1.37, -52.67) * mm});
            skLineSegment(sketch, "E360", {"start": v(-1.37, -52.67) * mm, "end": v(-1.13, -52.67) * mm});
            skLineSegment(sketch, "E361", {"start": v(-1.13, -52.67) * mm, "end": v(-0.88, -52.67) * mm});
            skLineSegment(sketch, "E362", {"start": v(-0.88, -52.67) * mm, "end": v(-0.64, -52.67) * mm});
            skLineSegment(sketch, "E363", {"start": v(-0.64, -52.67) * mm, "end": v(-0.4, -52.67) * mm});
            skLineSegment(sketch, "E364", {"start": v(-0.4, -52.67) * mm, "end": v(-0.15, -52.67) * mm});
            skLineSegment(sketch, "E365", {"start": v(-0.15, -52.67) * mm, "end": v(0.1, -52.67) * mm});
            skLineSegment(sketch, "E366", {"start": v(0.1, -52.67) * mm, "end": v(0.34, -52.67) * mm});
            skLineSegment(sketch, "E367", {"start": v(0.34, -52.67) * mm, "end": v(0.58, -52.67) * mm});
            skLineSegment(sketch, "E368", {"start": v(0.58, -52.67) * mm, "end": v(0.83, -52.67) * mm});
            skLineSegment(sketch, "E369", {"start": v(0.83, -52.67) * mm, "end": v(1.07, -52.67) * mm});
            skLineSegment(sketch, "E370", {"start": v(1.07, -52.67) * mm, "end": v(1.32, -52.67) * mm});
            skLineSegment(sketch, "E371", {"start": v(1.32, -52.67) * mm, "end": v(1.56, -52.67) * mm});
            skLineSegment(sketch, "E372", {"start": v(1.56, -52.67) * mm, "end": v(1.8, -52.67) * mm});
            skLineSegment(sketch, "E373", {"start": v(1.8, -52.67) * mm, "end": v(2.05, -52.67) * mm});
            skLineSegment(sketch, "E374", {"start": v(2.05, -52.67) * mm, "end": v(2.3, -52.67) * mm});
            skLineSegment(sketch, "E375", {"start": v(2.3, -52.67) * mm, "end": v(2.54, -52.67) * mm});
            skLineSegment(sketch, "E376", {"start": v(2.54, -52.67) * mm, "end": v(2.78, -52.67) * mm});
            skLineSegment(sketch, "E377", {"start": v(2.78, -52.67) * mm, "end": v(3.03, -52.67) * mm});
            skLineSegment(sketch, "E378", {"start": v(3.03, -52.67) * mm, "end": v(3.27, -52.67) * mm});
            skLineSegment(sketch, "E379", {"start": v(3.27, -52.67) * mm, "end": v(3.52, -52.67) * mm});
            skLineSegment(sketch, "E380", {"start": v(3.52, -52.67) * mm, "end": v(3.76, -52.67) * mm});
            skLineSegment(sketch, "E381", {"start": v(3.76, -52.67) * mm, "end": v(4, -52.67) * mm});
            skLineSegment(sketch, "E382", {"start": v(4, -52.67) * mm, "end": v(4.25, -52.67) * mm});
            skLineSegment(sketch, "E383", {"start": v(4.25, -52.67) * mm, "end": v(4.36, -52.67) * mm});
            skLineSegment(sketch, "E384", {"start": v(4.36, -52.67) * mm, "end": v(4.48, -52.67) * mm});
            skLineSegment(sketch, "E385", {"start": v(4.48, -52.67) * mm, "end": v(4.59, -52.67) * mm});
            skLineSegment(sketch, "E386", {"start": v(4.59, -52.67) * mm, "end": v(4.7, -52.67) * mm});
            skLineSegment(sketch, "E387", {"start": v(4.7, -52.67) * mm, "end": v(4.81, -52.67) * mm});
            skLineSegment(sketch, "E388", {"start": v(4.81, -52.67) * mm, "end": v(4.92, -52.67) * mm});
            skLineSegment(sketch, "E389", {"start": v(4.92, -52.67) * mm, "end": v(5.03, -52.67) * mm});
            skLineSegment(sketch, "E390", {"start": v(5.03, -52.67) * mm, "end": v(5.15, -52.67) * mm});
            skLineSegment(sketch, "E391", {"start": v(5.15, -52.67) * mm, "end": v(5.26, -52.67) * mm});
            skLineSegment(sketch, "E392", {"start": v(5.26, -52.67) * mm, "end": v(5.37, -52.67) * mm});
            skLineSegment(sketch, "E393", {"start": v(5.37, -52.67) * mm, "end": v(5.48, -52.67) * mm});
            skLineSegment(sketch, "E394", {"start": v(5.48, -52.67) * mm, "end": v(5.6, -52.67) * mm});
            skLineSegment(sketch, "E395", {"start": v(5.6, -52.67) * mm, "end": v(5.7, -52.67) * mm});
            skLineSegment(sketch, "E396", {"start": v(5.7, -52.67) * mm, "end": v(5.82, -52.67) * mm});
            skLineSegment(sketch, "E397", {"start": v(5.82, -52.67) * mm, "end": v(5.93, -52.67) * mm});
            skLineSegment(sketch, "E398", {"start": v(5.93, -52.67) * mm, "end": v(6.04, -52.67) * mm});
            skLineSegment(sketch, "E399", {"start": v(6.04, -52.67) * mm, "end": v(6.15, -52.67) * mm});
            skLineSegment(sketch, "E400", {"start": v(6.15, -52.67) * mm, "end": v(6.26, -52.67) * mm});
            skLineSegment(sketch, "E401", {"start": v(6.26, -52.67) * mm, "end": v(6.37, -52.67) * mm});
            skLineSegment(sketch, "E402", {"start": v(6.37, -52.67) * mm, "end": v(6.49, -52.67) * mm});
            skLineSegment(sketch, "E403", {"start": v(6.49, -52.67) * mm, "end": v(6.6, -52.67) * mm});
            skLineSegment(sketch, "E404", {"start": v(6.6, -52.67) * mm, "end": v(6.7, -52.67) * mm});
            skLineSegment(sketch, "E405", {"start": v(6.7, -52.67) * mm, "end": v(6.82, -52.67) * mm});
            skLineSegment(sketch, "E406", {"start": v(6.82, -52.67) * mm, "end": v(6.93, -52.67) * mm});
            skLineSegment(sketch, "E407", {"start": v(6.93, -52.67) * mm, "end": v(7.04, -52.67) * mm});
            skLineSegment(sketch, "E408", {"start": v(7.04, -52.67) * mm, "end": v(7.16, -52.67) * mm});
            skLineSegment(sketch, "E409", {"start": v(7.16, -52.67) * mm, "end": v(7.27, -52.67) * mm});
            skLineSegment(sketch, "E410", {"start": v(7.27, -52.67) * mm, "end": v(7.38, -52.67) * mm});
            skLineSegment(sketch, "E411", {"start": v(7.38, -52.67) * mm, "end": v(7.5, -52.67) * mm});
            skLineSegment(sketch, "E412", {"start": v(7.5, -52.67) * mm, "end": v(7.6, -52.67) * mm});
            skLineSegment(sketch, "E413", {"start": v(7.6, -52.67) * mm, "end": v(7.71, -52.67) * mm});
            skLineSegment(sketch, "E414", {"start": v(7.71, -52.67) * mm, "end": v(7.83, -52.67) * mm});
            skLineSegment(sketch, "E415", {"start": v(7.83, -52.67) * mm, "end": v(7.94, -52.67) * mm});
            skLineSegment(sketch, "E416", {"start": v(7.94, -52.67) * mm, "end": v(8.05, -52.67) * mm});
            skLineSegment(sketch, "E417", {"start": v(8.05, -52.67) * mm, "end": v(8.16, -52.67) * mm});
            skLineSegment(sketch, "E418", {"start": v(8.16, -52.67) * mm, "end": v(8.27, -52.67) * mm});
            skLineSegment(sketch, "E419", {"start": v(8.27, -52.67) * mm, "end": v(8.39, -52.67) * mm});
            skLineSegment(sketch, "E420", {"start": v(8.39, -52.67) * mm, "end": v(8.5, -52.67) * mm});
            skLineSegment(sketch, "E421", {"start": v(8.5, -52.67) * mm, "end": v(8.6, -52.67) * mm});
            skLineSegment(sketch, "E422", {"start": v(8.6, -52.67) * mm, "end": v(8.72, -52.67) * mm});
            skLineSegment(sketch, "E423", {"start": v(8.72, -52.67) * mm, "end": v(8.83, -52.67) * mm});
            skLineSegment(sketch, "E424", {"start": v(8.83, -52.67) * mm, "end": v(8.94, -52.67) * mm});
            skLineSegment(sketch, "E425", {"start": v(8.94, -52.67) * mm, "end": v(9.05, -52.67) * mm});
            skLineSegment(sketch, "E426", {"start": v(9.05, -52.67) * mm, "end": v(9.17, -52.67) * mm});
            skLineSegment(sketch, "E427", {"start": v(9.17, -52.67) * mm, "end": v(9.28, -52.67) * mm});
            skLineSegment(sketch, "E428", {"start": v(9.28, -52.67) * mm, "end": v(9.39, -52.67) * mm});
            skLineSegment(sketch, "E429", {"start": v(9.39, -52.67) * mm, "end": v(9.5, -52.67) * mm});
            skLineSegment(sketch, "E430", {"start": v(9.5, -52.67) * mm, "end": v(9.61, -52.67) * mm});
            skLineSegment(sketch, "E431", {"start": v(9.61, -52.67) * mm, "end": v(9.73, -52.67) * mm});
            skLineSegment(sketch, "E432", {"start": v(9.73, -52.67) * mm, "end": v(9.84, -52.67) * mm});
            skLineSegment(sketch, "E433", {"start": v(9.84, -52.67) * mm, "end": v(9.95, -52.67) * mm});
            skLineSegment(sketch, "E434", {"start": v(9.95, -52.67) * mm, "end": v(10.06, -52.67) * mm});
            skLineSegment(sketch, "E435", {"start": v(10.06, -52.67) * mm, "end": v(10.17, -52.67) * mm});
            skLineSegment(sketch, "E436", {"start": v(10.17, -52.67) * mm, "end": v(10.28, -52.67) * mm});
            skLineSegment(sketch, "E437", {"start": v(10.28, -52.67) * mm, "end": v(10.4, -52.67) * mm});
            skLineSegment(sketch, "E438", {"start": v(10.4, -52.67) * mm, "end": v(10.5, -52.67) * mm});
            skLineSegment(sketch, "E439", {"start": v(10.5, -52.67) * mm, "end": v(10.62, -52.67) * mm});
            skLineSegment(sketch, "E440", {"start": v(10.62, -52.67) * mm, "end": v(10.73, -52.67) * mm});
            skLineSegment(sketch, "E441", {"start": v(10.73, -52.67) * mm, "end": v(10.84, -52.67) * mm});
            skLineSegment(sketch, "E442", {"start": v(10.84, -52.67) * mm, "end": v(10.95, -52.67) * mm});
            skLineSegment(sketch, "E443", {"start": v(10.95, -52.67) * mm, "end": v(11.07, -52.67) * mm});
            skLineSegment(sketch, "E444", {"start": v(11.07, -52.67) * mm, "end": v(11.18, -52.67) * mm});
            skLineSegment(sketch, "E445", {"start": v(11.18, -52.67) * mm, "end": v(11.29, -52.67) * mm});
            skLineSegment(sketch, "E446", {"start": v(11.29, -52.67) * mm, "end": v(11.4, -52.67) * mm});
            skLineSegment(sketch, "E447", {"start": v(11.4, -52.67) * mm, "end": v(11.4, -52.34) * mm});
            skLineSegment(sketch, "E448", {"start": v(11.4, -52.34) * mm, "end": v(11.4, -52) * mm});
            skLineSegment(sketch, "E449", {"start": v(11.4, -52) * mm, "end": v(11.4, -51.67) * mm});
            skLineSegment(sketch, "E450", {"start": v(11.4, -51.67) * mm, "end": v(11.4, -51.34) * mm});
            skLineSegment(sketch, "E451", {"start": v(11.4, -51.34) * mm, "end": v(11.4, -51.01) * mm});
            skLineSegment(sketch, "E452", {"start": v(11.4, -51.01) * mm, "end": v(11.4, -50.68) * mm});
            skLineSegment(sketch, "E453", {"start": v(11.4, -50.68) * mm, "end": v(11.4, -50.35) * mm});
            skLineSegment(sketch, "E454", {"start": v(11.4, -50.35) * mm, "end": v(11.4, -50.02) * mm});
            skLineSegment(sketch, "E455", {"start": v(11.4, -50.02) * mm, "end": v(11.4, -49.7) * mm});
            skLineSegment(sketch, "E456", {"start": v(11.4, -49.7) * mm, "end": v(11.4, -49.36) * mm});
            skLineSegment(sketch, "E457", {"start": v(11.4, -49.36) * mm, "end": v(11.4, -49.03) * mm});
            skLineSegment(sketch, "E458", {"start": v(11.4, -49.03) * mm, "end": v(11.4, -48.7) * mm});
            skLineSegment(sketch, "E459", {"start": v(11.4, -48.7) * mm, "end": v(11.4, -48.37) * mm});
            skLineSegment(sketch, "E460", {"start": v(11.4, -48.37) * mm, "end": v(11.4, -48.04) * mm});
            skLineSegment(sketch, "E461", {"start": v(11.4, -48.04) * mm, "end": v(11.4, -47.71) * mm});
            skLineSegment(sketch, "E462", {"start": v(11.4, -47.71) * mm, "end": v(11.4, -47.38) * mm});
            skLineSegment(sketch, "E463", {"start": v(11.4, -47.38) * mm, "end": v(11.4, -47.05) * mm});
            skLineSegment(sketch, "E464", {"start": v(11.4, -47.05) * mm, "end": v(11.4, -46.72) * mm});
            skLineSegment(sketch, "E465", {"start": v(11.4, -46.72) * mm, "end": v(11.4, -46.4) * mm});
            skLineSegment(sketch, "E466", {"start": v(11.4, -46.4) * mm, "end": v(11.4, -46.06) * mm});
            skLineSegment(sketch, "E467", {"start": v(11.4, -46.06) * mm, "end": v(11.4, -45.73) * mm});
            skLineSegment(sketch, "E468", {"start": v(11.4, -45.73) * mm, "end": v(11.4, -45.4) * mm});
            skLineSegment(sketch, "E469", {"start": v(11.4, -45.4) * mm, "end": v(11.4, -45.07) * mm});
            skLineSegment(sketch, "E470", {"start": v(11.4, -45.07) * mm, "end": v(11.4, -44.74) * mm});
            skLineSegment(sketch, "E471", {"start": v(11.4, -44.74) * mm, "end": v(11.4, -44.4) * mm});
            skLineSegment(sketch, "E472", {"start": v(11.4, -44.4) * mm, "end": v(11.4, -44.08) * mm});
            skLineSegment(sketch, "E473", {"start": v(11.4, -44.08) * mm, "end": v(11.4, -43.75) * mm});
            skLineSegment(sketch, "E474", {"start": v(11.4, -43.75) * mm, "end": v(11.4, -43.42) * mm});
            skLineSegment(sketch, "E475", {"start": v(11.4, -43.42) * mm, "end": v(11.4, -43.09) * mm});
            skLineSegment(sketch, "E476", {"start": v(11.4, -43.09) * mm, "end": v(11.4, -42.76) * mm});
            skLineSegment(sketch, "E477", {"start": v(11.4, -42.76) * mm, "end": v(11.4, -42.43) * mm});
            skLineSegment(sketch, "E478", {"start": v(11.4, -42.43) * mm, "end": v(11.4, -42.1) * mm});
            skLineSegment(sketch, "E479", {"start": v(11.4, -42.1) * mm, "end": v(11.4, -41.77) * mm});
            skLineSegment(sketch, "E480", {"start": v(11.4, -41.77) * mm, "end": v(11.4, -41.44) * mm});
            skLineSegment(sketch, "E481", {"start": v(11.4, -41.44) * mm, "end": v(11.4, -41.1) * mm});
            skLineSegment(sketch, "E482", {"start": v(11.4, -41.1) * mm, "end": v(11.4, -40.78) * mm});
            skLineSegment(sketch, "E483", {"start": v(11.4, -40.78) * mm, "end": v(11.4, -40.45) * mm});
            skLineSegment(sketch, "E484", {"start": v(11.4, -40.45) * mm, "end": v(11.4, -40.12) * mm});
            skLineSegment(sketch, "E485", {"start": v(11.4, -40.12) * mm, "end": v(11.4, -39.79) * mm});
            skLineSegment(sketch, "E486", {"start": v(11.4, -39.79) * mm, "end": v(11.4, -39.46) * mm});
            skLineSegment(sketch, "E487", {"start": v(11.4, -39.46) * mm, "end": v(11.4, -39.13) * mm});
            skLineSegment(sketch, "E488", {"start": v(11.4, -39.13) * mm, "end": v(11.4, -38.8) * mm});
            skLineSegment(sketch, "E489", {"start": v(11.4, -38.8) * mm, "end": v(11.4, -38.47) * mm});
            skLineSegment(sketch, "E490", {"start": v(11.4, -38.47) * mm, "end": v(11.4, -38.14) * mm});
            skLineSegment(sketch, "E491", {"start": v(11.4, -38.14) * mm, "end": v(11.4, -37.8) * mm});
            skLineSegment(sketch, "E492", {"start": v(11.4, -37.8) * mm, "end": v(11.4, -37.47) * mm});
            skLineSegment(sketch, "E493", {"start": v(11.4, -37.47) * mm, "end": v(11.4, -37.14) * mm});
            skLineSegment(sketch, "E494", {"start": v(11.4, -37.14) * mm, "end": v(11.4, -36.81) * mm});
            skLineSegment(sketch, "E495", {"start": v(11.4, -36.81) * mm, "end": v(11.4, -36.48) * mm});
            skLineSegment(sketch, "E496", {"start": v(11.4, -36.48) * mm, "end": v(11.4, -36.15) * mm});
            skLineSegment(sketch, "E497", {"start": v(11.4, -36.15) * mm, "end": v(11.4, -35.82) * mm});
            skLineSegment(sketch, "E498", {"start": v(11.4, -35.82) * mm, "end": v(11.4, -35.5) * mm});
            skLineSegment(sketch, "E499", {"start": v(11.4, -35.5) * mm, "end": v(11.4, -35.16) * mm});
            skLineSegment(sketch, "E500", {"start": v(11.4, -35.16) * mm, "end": v(11.4, -34.83) * mm});
            skLineSegment(sketch, "E501", {"start": v(11.4, -34.83) * mm, "end": v(11.4, -34.5) * mm});
            skLineSegment(sketch, "E502", {"start": v(11.4, -34.5) * mm, "end": v(11.4, -34.17) * mm});
            skLineSegment(sketch, "E503", {"start": v(11.4, -34.17) * mm, "end": v(11.4, -33.84) * mm});
            skLineSegment(sketch, "E504", {"start": v(11.4, -33.84) * mm, "end": v(11.4, -33.51) * mm});
            skLineSegment(sketch, "E505", {"start": v(11.4, -33.51) * mm, "end": v(11.4, -33.18) * mm});
            skLineSegment(sketch, "E506", {"start": v(11.4, -33.18) * mm, "end": v(11.4, -32.85) * mm});
            skLineSegment(sketch, "E507", {"start": v(11.4, -32.85) * mm, "end": v(11.4, -32.52) * mm});
            skLineSegment(sketch, "E508", {"start": v(11.4, -32.52) * mm, "end": v(11.4, -32.2) * mm});
            skLineSegment(sketch, "E509", {"start": v(11.4, -32.2) * mm, "end": v(11.4, -31.86) * mm});
            skLineSegment(sketch, "E510", {"start": v(11.4, -31.86) * mm, "end": v(11.4, -31.53) * mm});
            skLineSegment(sketch, "E511", {"start": v(11.4, -31.53) * mm, "end": v(11.38, -31.53) * mm});
            skLineSegment(sketch, "E512", {"start": v(11.38, -31.53) * mm, "end": v(11.36, -31.53) * mm});
            skLineSegment(sketch, "E513", {"start": v(11.36, -31.53) * mm, "end": v(11.33, -31.53) * mm});
            skLineSegment(sketch, "E514", {"start": v(11.33, -31.53) * mm, "end": v(11.31, -31.53) * mm});
            skLineSegment(sketch, "E515", {"start": v(11.31, -31.53) * mm, "end": v(11.3, -31.54) * mm});
            skLineSegment(sketch, "E516", {"start": v(11.3, -31.54) * mm, "end": v(11.27, -31.54) * mm});
            skLineSegment(sketch, "E517", {"start": v(11.27, -31.54) * mm, "end": v(11.25, -31.54) * mm});
            skLineSegment(sketch, "E518", {"start": v(11.25, -31.54) * mm, "end": v(11.23, -31.55) * mm});
            skLineSegment(sketch, "E519", {"start": v(11.23, -31.55) * mm, "end": v(11.2, -31.55) * mm});
            skLineSegment(sketch, "E520", {"start": v(11.2, -31.55) * mm, "end": v(11.18, -31.56) * mm});
            skLineSegment(sketch, "E521", {"start": v(11.18, -31.56) * mm, "end": v(11.16, -31.56) * mm});
            skLineSegment(sketch, "E522", {"start": v(11.16, -31.56) * mm, "end": v(11.14, -31.57) * mm});
            skLineSegment(sketch, "E523", {"start": v(11.14, -31.57) * mm, "end": v(11.12, -31.58) * mm});
            skLineSegment(sketch, "E524", {"start": v(11.12, -31.58) * mm, "end": v(11.1, -31.58) * mm});
            skLineSegment(sketch, "E525", {"start": v(11.1, -31.58) * mm, "end": v(11.08, -31.6) * mm});
            skLineSegment(sketch, "E526", {"start": v(11.08, -31.6) * mm, "end": v(11.06, -31.6) * mm});
            skLineSegment(sketch, "E527", {"start": v(11.06, -31.6) * mm, "end": v(11.05, -31.6) * mm});
            skLineSegment(sketch, "E528", {"start": v(11.05, -31.6) * mm, "end": v(11.03, -31.62) * mm});
            skLineSegment(sketch, "E529", {"start": v(11.03, -31.62) * mm, "end": v(11, -31.62) * mm});
            skLineSegment(sketch, "E530", {"start": v(11, -31.62) * mm, "end": v(10.99, -31.63) * mm});
            skLineSegment(sketch, "E531", {"start": v(10.99, -31.63) * mm, "end": v(10.97, -31.64) * mm});
            skLineSegment(sketch, "E532", {"start": v(10.97, -31.64) * mm, "end": v(10.95, -31.65) * mm});
            skLineSegment(sketch, "E533", {"start": v(10.95, -31.65) * mm, "end": v(10.94, -31.67) * mm});
            skLineSegment(sketch, "E534", {"start": v(10.94, -31.67) * mm, "end": v(10.92, -31.68) * mm});
            skLineSegment(sketch, "E535", {"start": v(10.92, -31.68) * mm, "end": v(10.9, -31.69) * mm});
            skLineSegment(sketch, "E536", {"start": v(10.9, -31.69) * mm, "end": v(10.88, -31.7) * mm});
            skLineSegment(sketch, "E537", {"start": v(10.88, -31.7) * mm, "end": v(10.87, -31.71) * mm});
            skLineSegment(sketch, "E538", {"start": v(10.87, -31.71) * mm, "end": v(10.85, -31.73) * mm});
            skLineSegment(sketch, "E539", {"start": v(10.85, -31.73) * mm, "end": v(10.84, -31.74) * mm});
            skLineSegment(sketch, "E540", {"start": v(10.84, -31.74) * mm, "end": v(10.82, -31.75) * mm});
            skLineSegment(sketch, "E541", {"start": v(10.82, -31.75) * mm, "end": v(10.8, -31.77) * mm});
            skLineSegment(sketch, "E542", {"start": v(10.8, -31.77) * mm, "end": v(10.8, -31.78) * mm});
            skLineSegment(sketch, "E543", {"start": v(10.8, -31.78) * mm, "end": v(10.78, -31.8) * mm});
            skLineSegment(sketch, "E544", {"start": v(10.78, -31.8) * mm, "end": v(10.76, -31.81) * mm});
            skLineSegment(sketch, "E545", {"start": v(10.76, -31.81) * mm, "end": v(10.75, -31.83) * mm});
            skLineSegment(sketch, "E546", {"start": v(10.75, -31.83) * mm, "end": v(10.74, -31.84) * mm});
            skLineSegment(sketch, "E547", {"start": v(10.74, -31.84) * mm, "end": v(10.72, -31.86) * mm});
            skLineSegment(sketch, "E548", {"start": v(10.72, -31.86) * mm, "end": v(10.71, -31.88) * mm});
            skLineSegment(sketch, "E549", {"start": v(10.71, -31.88) * mm, "end": v(10.7, -31.9) * mm});
            skLineSegment(sketch, "E550", {"start": v(10.7, -31.9) * mm, "end": v(10.69, -31.91) * mm});
            skLineSegment(sketch, "E551", {"start": v(10.69, -31.91) * mm, "end": v(10.67, -31.93) * mm});
            skLineSegment(sketch, "E552", {"start": v(10.67, -31.93) * mm, "end": v(10.66, -31.95) * mm});
            skLineSegment(sketch, "E553", {"start": v(10.66, -31.95) * mm, "end": v(10.65, -31.96) * mm});
            skLineSegment(sketch, "E554", {"start": v(10.65, -31.96) * mm, "end": v(10.64, -31.98) * mm});
            skLineSegment(sketch, "E555", {"start": v(10.64, -31.98) * mm, "end": v(10.63, -32) * mm});
            skLineSegment(sketch, "E556", {"start": v(10.63, -32) * mm, "end": v(10.62, -32.02) * mm});
            skLineSegment(sketch, "E557", {"start": v(10.62, -32.02) * mm, "end": v(10.62, -32.04) * mm});
            skLineSegment(sketch, "E558", {"start": v(10.62, -32.04) * mm, "end": v(10.6, -32.06) * mm});
            skLineSegment(sketch, "E559", {"start": v(10.6, -32.06) * mm, "end": v(10.6, -32.08) * mm});
            skLineSegment(sketch, "E560", {"start": v(10.6, -32.08) * mm, "end": v(10.6, -32.1) * mm});
            skLineSegment(sketch, "E561", {"start": v(10.6, -32.1) * mm, "end": v(10.58, -32.12) * mm});
            skLineSegment(sketch, "E562", {"start": v(10.58, -32.12) * mm, "end": v(10.58, -32.14) * mm});
            skLineSegment(sketch, "E563", {"start": v(10.58, -32.14) * mm, "end": v(10.57, -32.16) * mm});
            skLineSegment(sketch, "E564", {"start": v(10.57, -32.16) * mm, "end": v(10.57, -32.18) * mm});
            skLineSegment(sketch, "E565", {"start": v(10.57, -32.18) * mm, "end": v(10.56, -32.2) * mm});
            skLineSegment(sketch, "E566", {"start": v(10.56, -32.2) * mm, "end": v(10.56, -32.22) * mm});
            skLineSegment(sketch, "E567", {"start": v(10.56, -32.22) * mm, "end": v(10.55, -32.24) * mm});
            skLineSegment(sketch, "E568", {"start": v(10.55, -32.24) * mm, "end": v(10.55, -32.26) * mm});
            skLineSegment(sketch, "E569", {"start": v(10.55, -32.26) * mm, "end": v(10.55, -32.28) * mm});
            skLineSegment(sketch, "E570", {"start": v(10.55, -32.28) * mm, "end": v(10.54, -32.3) * mm});
            skLineSegment(sketch, "E571", {"start": v(10.54, -32.3) * mm, "end": v(10.54, -32.33) * mm});
            skLineSegment(sketch, "E572", {"start": v(10.54, -32.33) * mm, "end": v(10.54, -32.35) * mm});
            skLineSegment(sketch, "E573", {"start": v(10.54, -32.35) * mm, "end": v(10.54, -32.37) * mm});
            skLineSegment(sketch, "E574", {"start": v(10.54, -32.37) * mm, "end": v(10.54, -32.4) * mm});
            skLineSegment(sketch, "E575", {"start": v(10.54, -32.4) * mm, "end": v(10.54, -32.4) * mm});
            skLineSegment(sketch, "E576", {"start": v(10.54, -32.4) * mm, "end": v(10.54, -32.41) * mm});
            skLineSegment(sketch, "E577", {"start": v(10.54, -32.41) * mm, "end": v(10.54, -32.42) * mm});
            skLineSegment(sketch, "E578", {"start": v(10.54, -32.42) * mm, "end": v(10.54, -32.42) * mm});
            skLineSegment(sketch, "E579", {"start": v(10.54, -32.42) * mm, "end": v(10.54, -32.43) * mm});
            skLineSegment(sketch, "E580", {"start": v(10.54, -32.43) * mm, "end": v(10.54, -32.43) * mm});
            skLineSegment(sketch, "E581", {"start": v(10.54, -32.43) * mm, "end": v(10.54, -32.44) * mm});
            skLineSegment(sketch, "E582", {"start": v(10.54, -32.44) * mm, "end": v(10.54, -32.44) * mm});
            skLineSegment(sketch, "E583", {"start": v(10.54, -32.44) * mm, "end": v(10.54, -32.45) * mm});
            skLineSegment(sketch, "E584", {"start": v(10.54, -32.45) * mm, "end": v(10.54, -32.45) * mm});
            skLineSegment(sketch, "E585", {"start": v(10.54, -32.45) * mm, "end": v(10.54, -32.46) * mm});
            skLineSegment(sketch, "E586", {"start": v(10.54, -32.46) * mm, "end": v(10.54, -32.46) * mm});
            skLineSegment(sketch, "E587", {"start": v(10.54, -32.46) * mm, "end": v(10.54, -32.47) * mm});
            skLineSegment(sketch, "E588", {"start": v(10.54, -32.47) * mm, "end": v(10.54, -32.47) * mm});
            skLineSegment(sketch, "E589", {"start": v(10.54, -32.47) * mm, "end": v(10.54, -32.48) * mm});
            skLineSegment(sketch, "E590", {"start": v(10.54, -32.48) * mm, "end": v(10.54, -32.48) * mm});
            skLineSegment(sketch, "E591", {"start": v(10.54, -32.48) * mm, "end": v(10.54, -32.49) * mm});
            skLineSegment(sketch, "E592", {"start": v(10.54, -32.49) * mm, "end": v(10.54, -32.5) * mm});
            skLineSegment(sketch, "E593", {"start": v(10.54, -32.5) * mm, "end": v(10.54, -32.5) * mm});
            skLineSegment(sketch, "E594", {"start": v(10.54, -32.5) * mm, "end": v(10.54, -32.51) * mm});
            skLineSegment(sketch, "E595", {"start": v(10.54, -32.51) * mm, "end": v(10.54, -32.52) * mm});
            skLineSegment(sketch, "E596", {"start": v(10.54, -32.52) * mm, "end": v(10.54, -32.52) * mm});
            skLineSegment(sketch, "E597", {"start": v(10.54, -32.52) * mm, "end": v(10.54, -32.53) * mm});
            skLineSegment(sketch, "E598", {"start": v(10.54, -32.53) * mm, "end": v(10.54, -32.53) * mm});
            skLineSegment(sketch, "E599", {"start": v(10.54, -32.53) * mm, "end": v(10.54, -32.54) * mm});
            skLineSegment(sketch, "E600", {"start": v(10.54, -32.54) * mm, "end": v(10.54, -32.54) * mm});
            skLineSegment(sketch, "E601", {"start": v(10.54, -32.54) * mm, "end": v(10.54, -32.55) * mm});
            skLineSegment(sketch, "E602", {"start": v(10.54, -32.55) * mm, "end": v(10.54, -32.55) * mm});
            skLineSegment(sketch, "E603", {"start": v(10.54, -32.55) * mm, "end": v(10.54, -32.56) * mm});
            skLineSegment(sketch, "E604", {"start": v(10.54, -32.56) * mm, "end": v(10.54, -32.56) * mm});
            skLineSegment(sketch, "E605", {"start": v(10.54, -32.56) * mm, "end": v(10.54, -32.57) * mm});
            skLineSegment(sketch, "E606", {"start": v(10.54, -32.57) * mm, "end": v(10.54, -32.57) * mm});
            skLineSegment(sketch, "E607", {"start": v(10.54, -32.57) * mm, "end": v(10.54, -32.58) * mm});
            skLineSegment(sketch, "E608", {"start": v(10.54, -32.58) * mm, "end": v(10.54, -32.58) * mm});
            skLineSegment(sketch, "E609", {"start": v(10.54, -32.58) * mm, "end": v(10.54, -32.59) * mm});
            skLineSegment(sketch, "E610", {"start": v(10.54, -32.59) * mm, "end": v(10.54, -32.6) * mm});
            skLineSegment(sketch, "E611", {"start": v(10.54, -32.6) * mm, "end": v(10.54, -32.6) * mm});
            skLineSegment(sketch, "E612", {"start": v(10.54, -32.6) * mm, "end": v(10.54, -32.61) * mm});
            skLineSegment(sketch, "E613", {"start": v(10.54, -32.61) * mm, "end": v(10.54, -32.62) * mm});
            skLineSegment(sketch, "E614", {"start": v(10.54, -32.62) * mm, "end": v(10.54, -32.62) * mm});
            skLineSegment(sketch, "E615", {"start": v(10.54, -32.62) * mm, "end": v(10.54, -32.63) * mm});
            skLineSegment(sketch, "E616", {"start": v(10.54, -32.63) * mm, "end": v(10.54, -32.63) * mm});
            skLineSegment(sketch, "E617", {"start": v(10.54, -32.63) * mm, "end": v(10.54, -32.64) * mm});
            skLineSegment(sketch, "E618", {"start": v(10.54, -32.64) * mm, "end": v(10.54, -32.64) * mm});
            skLineSegment(sketch, "E619", {"start": v(10.54, -32.64) * mm, "end": v(10.54, -32.65) * mm});
            skLineSegment(sketch, "E620", {"start": v(10.54, -32.65) * mm, "end": v(10.53, -32.65) * mm});
            skLineSegment(sketch, "E621", {"start": v(10.53, -32.65) * mm, "end": v(10.51, -32.66) * mm});
            skLineSegment(sketch, "E622", {"start": v(10.51, -32.66) * mm, "end": v(10.5, -32.67) * mm});
            skLineSegment(sketch, "E623", {"start": v(10.5, -32.67) * mm, "end": v(10.49, -32.67) * mm});
            skLineSegment(sketch, "E624", {"start": v(10.49, -32.67) * mm, "end": v(10.47, -32.68) * mm});
            skLineSegment(sketch, "E625", {"start": v(10.47, -32.68) * mm, "end": v(10.46, -32.69) * mm});
            skLineSegment(sketch, "E626", {"start": v(10.46, -32.69) * mm, "end": v(10.45, -32.7) * mm});
            skLineSegment(sketch, "E627", {"start": v(10.45, -32.7) * mm, "end": v(10.44, -32.7) * mm});
            skLineSegment(sketch, "E628", {"start": v(10.44, -32.7) * mm, "end": v(10.42, -32.7) * mm});
            skLineSegment(sketch, "E629", {"start": v(10.42, -32.7) * mm, "end": v(10.41, -32.71) * mm});
            skLineSegment(sketch, "E630", {"start": v(10.41, -32.71) * mm, "end": v(10.4, -32.72) * mm});
            skLineSegment(sketch, "E631", {"start": v(10.4, -32.72) * mm, "end": v(10.39, -32.73) * mm});
            skLineSegment(sketch, "E632", {"start": v(10.39, -32.73) * mm, "end": v(10.37, -32.73) * mm});
            skLineSegment(sketch, "E633", {"start": v(10.37, -32.73) * mm, "end": v(10.36, -32.74) * mm});
            skLineSegment(sketch, "E634", {"start": v(10.36, -32.74) * mm, "end": v(10.35, -32.75) * mm});
            skLineSegment(sketch, "E635", {"start": v(10.35, -32.75) * mm, "end": v(10.34, -32.76) * mm});
            skLineSegment(sketch, "E636", {"start": v(10.34, -32.76) * mm, "end": v(10.33, -32.76) * mm});
            skLineSegment(sketch, "E637", {"start": v(10.33, -32.76) * mm, "end": v(10.31, -32.77) * mm});
            skLineSegment(sketch, "E638", {"start": v(10.31, -32.77) * mm, "end": v(10.3, -32.78) * mm});
            skLineSegment(sketch, "E639", {"start": v(10.3, -32.78) * mm, "end": v(10.3, -32.79) * mm});
            skLineSegment(sketch, "E640", {"start": v(10.3, -32.79) * mm, "end": v(10.28, -32.8) * mm});
            skLineSegment(sketch, "E641", {"start": v(10.28, -32.8) * mm, "end": v(10.27, -32.8) * mm});
            skLineSegment(sketch, "E642", {"start": v(10.27, -32.8) * mm, "end": v(10.26, -32.81) * mm});
            skLineSegment(sketch, "E643", {"start": v(10.26, -32.81) * mm, "end": v(10.25, -32.82) * mm});
            skLineSegment(sketch, "E644", {"start": v(10.25, -32.82) * mm, "end": v(10.23, -32.83) * mm});
            skLineSegment(sketch, "E645", {"start": v(10.23, -32.83) * mm, "end": v(10.22, -32.83) * mm});
            skLineSegment(sketch, "E646", {"start": v(10.22, -32.83) * mm, "end": v(10.21, -32.84) * mm});
            skLineSegment(sketch, "E647", {"start": v(10.21, -32.84) * mm, "end": v(10.2, -32.85) * mm});
            skLineSegment(sketch, "E648", {"start": v(10.2, -32.85) * mm, "end": v(10.2, -32.86) * mm});
            skLineSegment(sketch, "E649", {"start": v(10.2, -32.86) * mm, "end": v(10.18, -32.87) * mm});
            skLineSegment(sketch, "E650", {"start": v(10.18, -32.87) * mm, "end": v(10.17, -32.88) * mm});
            skLineSegment(sketch, "E651", {"start": v(10.17, -32.88) * mm, "end": v(10.16, -32.89) * mm});
            skLineSegment(sketch, "E652", {"start": v(10.16, -32.89) * mm, "end": v(10.15, -32.9) * mm});
            skLineSegment(sketch, "E653", {"start": v(10.15, -32.9) * mm, "end": v(10.14, -32.9) * mm});
            skLineSegment(sketch, "E654", {"start": v(10.14, -32.9) * mm, "end": v(10.13, -32.91) * mm});
            skLineSegment(sketch, "E655", {"start": v(10.13, -32.91) * mm, "end": v(10.12, -32.92) * mm});
            skLineSegment(sketch, "E656", {"start": v(10.12, -32.92) * mm, "end": v(10.1, -32.93) * mm});
            skLineSegment(sketch, "E657", {"start": v(10.1, -32.93) * mm, "end": v(10.1, -32.94) * mm});
            skLineSegment(sketch, "E658", {"start": v(10.1, -32.94) * mm, "end": v(10.09, -32.95) * mm});
            skLineSegment(sketch, "E659", {"start": v(10.09, -32.95) * mm, "end": v(10.08, -32.96) * mm});
            skLineSegment(sketch, "E660", {"start": v(10.08, -32.96) * mm, "end": v(10.07, -32.97) * mm});
            skLineSegment(sketch, "E661", {"start": v(10.07, -32.97) * mm, "end": v(10.06, -32.98) * mm});
            skLineSegment(sketch, "E662", {"start": v(10.06, -32.98) * mm, "end": v(10.05, -32.99) * mm});
            skLineSegment(sketch, "E663", {"start": v(10.05, -32.99) * mm, "end": v(10.04, -33) * mm});
            skLineSegment(sketch, "E664", {"start": v(10.04, -33) * mm, "end": v(10.03, -33) * mm});
            skLineSegment(sketch, "E665", {"start": v(10.03, -33) * mm, "end": v(10.03, -33.01) * mm});
            skLineSegment(sketch, "E666", {"start": v(10.03, -33.01) * mm, "end": v(10.02, -33.02) * mm});
            skLineSegment(sketch, "E667", {"start": v(10.02, -33.02) * mm, "end": v(10, -33.03) * mm});
            skLineSegment(sketch, "E668", {"start": v(10, -33.03) * mm, "end": v(10, -33.04) * mm});
            skLineSegment(sketch, "E669", {"start": v(10, -33.04) * mm, "end": v(10, -33.05) * mm});
            skLineSegment(sketch, "E670", {"start": v(10, -33.05) * mm, "end": v(9.98, -33.06) * mm});
            skLineSegment(sketch, "E671", {"start": v(9.98, -33.06) * mm, "end": v(9.97, -33.07) * mm});
            skLineSegment(sketch, "E672", {"start": v(9.97, -33.07) * mm, "end": v(9.97, -33.08) * mm});
            skLineSegment(sketch, "E673", {"start": v(9.97, -33.08) * mm, "end": v(9.96, -33.1) * mm});
            skLineSegment(sketch, "E674", {"start": v(9.96, -33.1) * mm, "end": v(9.95, -33.1) * mm});
            skLineSegment(sketch, "E675", {"start": v(9.95, -33.1) * mm, "end": v(9.94, -33.11) * mm});
            skLineSegment(sketch, "E676", {"start": v(9.94, -33.11) * mm, "end": v(9.94, -33.13) * mm});
            skLineSegment(sketch, "E677", {"start": v(9.94, -33.13) * mm, "end": v(9.93, -33.14) * mm});
            skLineSegment(sketch, "E678", {"start": v(9.93, -33.14) * mm, "end": v(9.92, -33.15) * mm});
            skLineSegment(sketch, "E679", {"start": v(9.92, -33.15) * mm, "end": v(9.91, -33.16) * mm});
            skLineSegment(sketch, "E680", {"start": v(9.91, -33.16) * mm, "end": v(9.9, -33.17) * mm});
            skLineSegment(sketch, "E681", {"start": v(9.9, -33.17) * mm, "end": v(9.9, -33.18) * mm});
            skLineSegment(sketch, "E682", {"start": v(9.9, -33.18) * mm, "end": v(9.9, -33.19) * mm});
            skLineSegment(sketch, "E683", {"start": v(9.9, -33.19) * mm, "end": v(9.89, -33.2) * mm});
            skLineSegment(sketch, "E684", {"start": v(9.89, -33.2) * mm, "end": v(9.72, -33.23) * mm});
            skLineSegment(sketch, "E685", {"start": v(9.72, -33.23) * mm, "end": v(9.55, -33.27) * mm});
            skLineSegment(sketch, "E686", {"start": v(9.55, -33.27) * mm, "end": v(9.38, -33.32) * mm});
            skLineSegment(sketch, "E687", {"start": v(9.38, -33.32) * mm, "end": v(9.22, -33.36) * mm});
            skLineSegment(sketch, "E688", {"start": v(9.22, -33.36) * mm, "end": v(9.06, -33.41) * mm});
            skLineSegment(sketch, "E689", {"start": v(9.06, -33.41) * mm, "end": v(8.9, -33.46) * mm});
            skLineSegment(sketch, "E690", {"start": v(8.9, -33.46) * mm, "end": v(8.74, -33.52) * mm});
            skLineSegment(sketch, "E691", {"start": v(8.74, -33.52) * mm, "end": v(8.58, -33.58) * mm});
            skLineSegment(sketch, "E692", {"start": v(8.58, -33.58) * mm, "end": v(8.42, -33.64) * mm});
            skLineSegment(sketch, "E693", {"start": v(8.42, -33.64) * mm, "end": v(8.27, -33.7) * mm});
            skLineSegment(sketch, "E694", {"start": v(8.27, -33.7) * mm, "end": v(8.12, -33.78) * mm});
            skLineSegment(sketch, "E695", {"start": v(8.12, -33.78) * mm, "end": v(7.97, -33.85) * mm});
            skLineSegment(sketch, "E696", {"start": v(7.97, -33.85) * mm, "end": v(7.82, -33.92) * mm});
            skLineSegment(sketch, "E697", {"start": v(7.82, -33.92) * mm, "end": v(7.67, -34) * mm});
            skLineSegment(sketch, "E698", {"start": v(7.67, -34) * mm, "end": v(7.53, -34.08) * mm});
            skLineSegment(sketch, "E699", {"start": v(7.53, -34.08) * mm, "end": v(7.38, -34.17) * mm});
            skLineSegment(sketch, "E700", {"start": v(7.38, -34.17) * mm, "end": v(7.24, -34.25) * mm});
            skLineSegment(sketch, "E701", {"start": v(7.24, -34.25) * mm, "end": v(7.1, -34.34) * mm});
            skLineSegment(sketch, "E702", {"start": v(7.1, -34.34) * mm, "end": v(6.97, -34.44) * mm});
            skLineSegment(sketch, "E703", {"start": v(6.97, -34.44) * mm, "end": v(6.84, -34.53) * mm});
            skLineSegment(sketch, "E704", {"start": v(6.84, -34.53) * mm, "end": v(6.7, -34.63) * mm});
            skLineSegment(sketch, "E705", {"start": v(6.7, -34.63) * mm, "end": v(6.57, -34.73) * mm});
            skLineSegment(sketch, "E706", {"start": v(6.57, -34.73) * mm, "end": v(6.45, -34.83) * mm});
            skLineSegment(sketch, "E707", {"start": v(6.45, -34.83) * mm, "end": v(6.32, -34.94) * mm});
            skLineSegment(sketch, "E708", {"start": v(6.32, -34.94) * mm, "end": v(6.2, -35.05) * mm});
            skLineSegment(sketch, "E709", {"start": v(6.2, -35.05) * mm, "end": v(6.08, -35.16) * mm});
            skLineSegment(sketch, "E710", {"start": v(6.08, -35.16) * mm, "end": v(5.96, -35.27) * mm});
            skLineSegment(sketch, "E711", {"start": v(5.96, -35.27) * mm, "end": v(5.85, -35.39) * mm});
            skLineSegment(sketch, "E712", {"start": v(5.85, -35.39) * mm, "end": v(5.73, -35.5) * mm});
            skLineSegment(sketch, "E713", {"start": v(5.73, -35.5) * mm, "end": v(5.62, -35.63) * mm});
            skLineSegment(sketch, "E714", {"start": v(5.62, -35.63) * mm, "end": v(5.52, -35.75) * mm});
            skLineSegment(sketch, "E715", {"start": v(5.52, -35.75) * mm, "end": v(5.41, -35.88) * mm});
            skLineSegment(sketch, "E716", {"start": v(5.41, -35.88) * mm, "end": v(5.3, -36) * mm});
            skLineSegment(sketch, "E717", {"start": v(5.3, -36) * mm, "end": v(5.2, -36.13) * mm});
            skLineSegment(sketch, "E718", {"start": v(5.2, -36.13) * mm, "end": v(5.11, -36.26) * mm});
            skLineSegment(sketch, "E719", {"start": v(5.11, -36.26) * mm, "end": v(5.02, -36.4) * mm});
            skLineSegment(sketch, "E720", {"start": v(5.02, -36.4) * mm, "end": v(4.93, -36.53) * mm});
            skLineSegment(sketch, "E721", {"start": v(4.93, -36.53) * mm, "end": v(4.84, -36.67) * mm});
            skLineSegment(sketch, "E722", {"start": v(4.84, -36.67) * mm, "end": v(4.75, -36.81) * mm});
            skLineSegment(sketch, "E723", {"start": v(4.75, -36.81) * mm, "end": v(4.67, -36.95) * mm});
            skLineSegment(sketch, "E724", {"start": v(4.67, -36.95) * mm, "end": v(4.59, -37.1) * mm});
            skLineSegment(sketch, "E725", {"start": v(4.59, -37.1) * mm, "end": v(4.51, -37.24) * mm});
            skLineSegment(sketch, "E726", {"start": v(4.51, -37.24) * mm, "end": v(4.44, -37.39) * mm});
            skLineSegment(sketch, "E727", {"start": v(4.44, -37.39) * mm, "end": v(4.37, -37.54) * mm});
            skLineSegment(sketch, "E728", {"start": v(4.37, -37.54) * mm, "end": v(4.3, -37.69) * mm});
            skLineSegment(sketch, "E729", {"start": v(4.3, -37.69) * mm, "end": v(4.24, -37.84) * mm});
            skLineSegment(sketch, "E730", {"start": v(4.24, -37.84) * mm, "end": v(4.17, -38) * mm});
            skLineSegment(sketch, "E731", {"start": v(4.17, -38) * mm, "end": v(4.12, -38.15) * mm});
            skLineSegment(sketch, "E732", {"start": v(4.12, -38.15) * mm, "end": v(4.06, -38.3) * mm});
            skLineSegment(sketch, "E733", {"start": v(4.06, -38.3) * mm, "end": v(4, -38.46) * mm});
            skLineSegment(sketch, "E734", {"start": v(4, -38.46) * mm, "end": v(3.96, -38.62) * mm});
            skLineSegment(sketch, "E735", {"start": v(3.96, -38.62) * mm, "end": v(3.92, -38.78) * mm});
            skLineSegment(sketch, "E736", {"start": v(3.92, -38.78) * mm, "end": v(3.88, -38.94) * mm});
            skLineSegment(sketch, "E737", {"start": v(3.88, -38.94) * mm, "end": v(3.84, -39.1) * mm});
            skLineSegment(sketch, "E738", {"start": v(3.84, -39.1) * mm, "end": v(3.8, -39.27) * mm});
            skLineSegment(sketch, "E739", {"start": v(3.8, -39.27) * mm, "end": v(3.77, -39.44) * mm});
            skLineSegment(sketch, "E740", {"start": v(3.77, -39.44) * mm, "end": v(3.74, -39.6) * mm});
            skLineSegment(sketch, "E741", {"start": v(3.74, -39.6) * mm, "end": v(3.72, -39.77) * mm});
            skLineSegment(sketch, "E742", {"start": v(3.72, -39.77) * mm, "end": v(3.7, -39.94) * mm});
            skLineSegment(sketch, "E743", {"start": v(3.7, -39.94) * mm, "end": v(3.68, -40.1) * mm});
            skLineSegment(sketch, "E744", {"start": v(3.68, -40.1) * mm, "end": v(3.67, -40.28) * mm});
            skLineSegment(sketch, "E745", {"start": v(3.67, -40.28) * mm, "end": v(3.66, -40.45) * mm});
            skLineSegment(sketch, "E746", {"start": v(3.66, -40.45) * mm, "end": v(3.65, -40.62) * mm});
            skLineSegment(sketch, "E747", {"start": v(3.65, -40.62) * mm, "end": v(3.65, -40.8) * mm});
            skLineSegment(sketch, "E748", {"start": v(3.65, -40.8) * mm, "end": v(3.65, -40.97) * mm});
            skLineSegment(sketch, "E749", {"start": v(3.65, -40.97) * mm, "end": v(3.65, -41.15) * mm});
            skLineSegment(sketch, "E750", {"start": v(3.65, -41.15) * mm, "end": v(3.65, -41.33) * mm});
            skLineSegment(sketch, "E751", {"start": v(3.65, -41.33) * mm, "end": v(3.65, -41.5) * mm});
            skLineSegment(sketch, "E752", {"start": v(3.65, -41.5) * mm, "end": v(3.65, -41.68) * mm});
            skLineSegment(sketch, "E753", {"start": v(3.65, -41.68) * mm, "end": v(3.65, -41.85) * mm});
            skLineSegment(sketch, "E754", {"start": v(3.65, -41.85) * mm, "end": v(3.65, -42.03) * mm});
            skLineSegment(sketch, "E755", {"start": v(3.65, -42.03) * mm, "end": v(3.65, -42.2) * mm});
            skLineSegment(sketch, "E756", {"start": v(3.65, -42.2) * mm, "end": v(3.65, -42.38) * mm});
            skLineSegment(sketch, "E757", {"start": v(3.65, -42.38) * mm, "end": v(3.65, -42.56) * mm});
            skLineSegment(sketch, "E758", {"start": v(3.65, -42.56) * mm, "end": v(3.65, -42.73) * mm});
            skLineSegment(sketch, "E759", {"start": v(3.65, -42.73) * mm, "end": v(3.65, -42.91) * mm});
            skLineSegment(sketch, "E760", {"start": v(3.65, -42.91) * mm, "end": v(3.65, -43.09) * mm});
            skLineSegment(sketch, "E761", {"start": v(3.65, -43.09) * mm, "end": v(3.65, -43.26) * mm});
            skLineSegment(sketch, "E762", {"start": v(3.65, -43.26) * mm, "end": v(3.65, -43.44) * mm});
            skLineSegment(sketch, "E763", {"start": v(3.65, -43.44) * mm, "end": v(3.65, -43.61) * mm});
            skLineSegment(sketch, "E764", {"start": v(3.65, -43.61) * mm, "end": v(3.65, -43.8) * mm});
            skLineSegment(sketch, "E765", {"start": v(3.65, -43.8) * mm, "end": v(3.65, -43.97) * mm});
            skLineSegment(sketch, "E766", {"start": v(3.65, -43.97) * mm, "end": v(3.65, -44.14) * mm});
            skLineSegment(sketch, "E767", {"start": v(3.65, -44.14) * mm, "end": v(3.65, -44.32) * mm});
            skLineSegment(sketch, "E768", {"start": v(3.65, -44.32) * mm, "end": v(3.65, -44.5) * mm});
            skLineSegment(sketch, "E769", {"start": v(3.65, -44.5) * mm, "end": v(3.65, -44.67) * mm});
            skLineSegment(sketch, "E770", {"start": v(3.65, -44.67) * mm, "end": v(3.65, -44.85) * mm});
            skLineSegment(sketch, "E771", {"start": v(3.65, -44.85) * mm, "end": v(3.65, -45.02) * mm});
            skLineSegment(sketch, "E772", {"start": v(3.65, -45.02) * mm, "end": v(3.65, -45.2) * mm});
            skLineSegment(sketch, "E773", {"start": v(3.65, -45.2) * mm, "end": v(3.65, -45.38) * mm});
            skLineSegment(sketch, "E774", {"start": v(3.65, -45.38) * mm, "end": v(3.65, -45.55) * mm});
            skLineSegment(sketch, "E775", {"start": v(3.65, -45.55) * mm, "end": v(3.65, -45.73) * mm});
            skLineSegment(sketch, "E776", {"start": v(3.65, -45.73) * mm, "end": v(3.65, -45.9) * mm});
            skLineSegment(sketch, "E777", {"start": v(3.65, -45.9) * mm, "end": v(3.65, -46.08) * mm});
            skLineSegment(sketch, "E778", {"start": v(3.65, -46.08) * mm, "end": v(3.65, -46.26) * mm});
            skLineSegment(sketch, "E779", {"start": v(3.65, -46.26) * mm, "end": v(3.65, -46.43) * mm});
            skLineSegment(sketch, "E780", {"start": v(3.65, -46.43) * mm, "end": v(3.65, -46.6) * mm});
            skLineSegment(sketch, "E781", {"start": v(3.65, -46.6) * mm, "end": v(3.65, -46.78) * mm});
            skLineSegment(sketch, "E782", {"start": v(3.65, -46.78) * mm, "end": v(3.65, -46.96) * mm});
            skLineSegment(sketch, "E783", {"start": v(3.65, -46.96) * mm, "end": v(3.65, -47.14) * mm});
            skLineSegment(sketch, "E784", {"start": v(3.65, -47.14) * mm, "end": v(3.65, -47.31) * mm});
            skLineSegment(sketch, "E785", {"start": v(3.65, -47.31) * mm, "end": v(3.65, -47.49) * mm});
            skLineSegment(sketch, "E786", {"start": v(3.65, -47.49) * mm, "end": v(3.65, -47.66) * mm});
            skLineSegment(sketch, "E787", {"start": v(3.65, -47.66) * mm, "end": v(3.65, -47.84) * mm});
            skLineSegment(sketch, "E788", {"start": v(3.65, -47.84) * mm, "end": v(3.65, -48.02) * mm});
            skLineSegment(sketch, "E789", {"start": v(3.65, -48.02) * mm, "end": v(3.65, -48.2) * mm});
            skLineSegment(sketch, "E790", {"start": v(3.65, -48.2) * mm, "end": v(3.65, -48.37) * mm});
            skLineSegment(sketch, "E791", {"start": v(3.65, -48.37) * mm, "end": v(3.65, -48.54) * mm});
            skLineSegment(sketch, "E792", {"start": v(3.65, -48.54) * mm, "end": v(3.65, -48.72) * mm});
            skLineSegment(sketch, "E793", {"start": v(3.65, -48.72) * mm, "end": v(3.65, -48.9) * mm});
            skLineSegment(sketch, "E794", {"start": v(3.65, -48.9) * mm, "end": v(3.65, -49.07) * mm});
            skLineSegment(sketch, "E795", {"start": v(3.65, -49.07) * mm, "end": v(3.65, -49.25) * mm});
            skLineSegment(sketch, "E796", {"start": v(3.65, -49.25) * mm, "end": v(3.65, -49.42) * mm});
            skLineSegment(sketch, "E797", {"start": v(3.65, -49.42) * mm, "end": v(3.65, -49.6) * mm});
            skLineSegment(sketch, "E798", {"start": v(3.65, -49.6) * mm, "end": v(3.65, -49.78) * mm});
            skLineSegment(sketch, "E799", {"start": v(3.65, -49.78) * mm, "end": v(3.65, -49.95) * mm});
            skLineSegment(sketch, "E800", {"start": v(3.65, -49.95) * mm, "end": v(3.65, -50.13) * mm});
            skLineSegment(sketch, "E801", {"start": v(3.65, -50.13) * mm, "end": v(3.65, -50.3) * mm});
            skLineSegment(sketch, "E802", {"start": v(3.65, -50.3) * mm, "end": v(3.65, -50.48) * mm});
            skLineSegment(sketch, "E803", {"start": v(3.65, -50.48) * mm, "end": v(3.65, -50.66) * mm});
            skLineSegment(sketch, "E804", {"start": v(3.65, -50.66) * mm, "end": v(3.65, -50.83) * mm});
            skLineSegment(sketch, "E805", {"start": v(3.65, -50.83) * mm, "end": v(3.65, -51) * mm});
            skLineSegment(sketch, "E806", {"start": v(3.65, -51) * mm, "end": v(3.65, -51.18) * mm});
            skLineSegment(sketch, "E807", {"start": v(3.65, -51.18) * mm, "end": v(3.65, -51.36) * mm});
            skLineSegment(sketch, "E808", {"start": v(3.65, -51.36) * mm, "end": v(3.65, -51.54) * mm});
            skLineSegment(sketch, "E809", {"start": v(3.65, -51.54) * mm, "end": v(3.65, -51.71) * mm});
            skLineSegment(sketch, "E810", {"start": v(3.65, -51.71) * mm, "end": v(3.65, -51.89) * mm});
            skLineSegment(sketch, "E811", {"start": v(3.65, -51.89) * mm, "end": v(3.65, -52.07) * mm});
            skLineSegment(sketch, "E812", {"start": v(3.65, -52.07) * mm, "end": v(3.43, -52.07) * mm});
            skLineSegment(sketch, "E813", {"start": v(3.43, -52.07) * mm, "end": v(3.2, -52.07) * mm});
            skLineSegment(sketch, "E814", {"start": v(3.2, -52.07) * mm, "end": v(2.97, -52.07) * mm});
            skLineSegment(sketch, "E815", {"start": v(2.97, -52.07) * mm, "end": v(2.75, -52.07) * mm});
            skLineSegment(sketch, "E816", {"start": v(2.75, -52.07) * mm, "end": v(2.52, -52.07) * mm});
            skLineSegment(sketch, "E817", {"start": v(2.52, -52.07) * mm, "end": v(2.3, -52.07) * mm});
            skLineSegment(sketch, "E818", {"start": v(2.3, -52.07) * mm, "end": v(2.07, -52.07) * mm});
            skLineSegment(sketch, "E819", {"start": v(2.07, -52.07) * mm, "end": v(1.85, -52.07) * mm});
            skLineSegment(sketch, "E820", {"start": v(1.85, -52.07) * mm, "end": v(1.62, -52.07) * mm});
            skLineSegment(sketch, "E821", {"start": v(1.62, -52.07) * mm, "end": v(1.4, -52.07) * mm});
            skLineSegment(sketch, "E822", {"start": v(1.4, -52.07) * mm, "end": v(1.17, -52.07) * mm});
            skLineSegment(sketch, "E823", {"start": v(1.17, -52.07) * mm, "end": v(0.94, -52.07) * mm});
            skLineSegment(sketch, "E824", {"start": v(0.94, -52.07) * mm, "end": v(0.72, -52.07) * mm});
            skLineSegment(sketch, "E825", {"start": v(0.72, -52.07) * mm, "end": v(0.5, -52.07) * mm});
            skLineSegment(sketch, "E826", {"start": v(0.5, -52.07) * mm, "end": v(0.26, -52.07) * mm});
            skLineSegment(sketch, "E827", {"start": v(0.26, -52.07) * mm, "end": v(0.04, -52.07) * mm});
            skLineSegment(sketch, "E828", {"start": v(0.04, -52.07) * mm, "end": v(-0.19, -52.07) * mm});
            skLineSegment(sketch, "E829", {"start": v(-0.19, -52.07) * mm, "end": v(-0.41, -52.07) * mm});
            skLineSegment(sketch, "E830", {"start": v(-0.41, -52.07) * mm, "end": v(-0.64, -52.07) * mm});
            skLineSegment(sketch, "E831", {"start": v(-0.64, -52.07) * mm, "end": v(-0.86, -52.07) * mm});
            skLineSegment(sketch, "E832", {"start": v(-0.86, -52.07) * mm, "end": v(-1.1, -52.07) * mm});
            skLineSegment(sketch, "E833", {"start": v(-1.1, -52.07) * mm, "end": v(-1.32, -52.07) * mm});
            skLineSegment(sketch, "E834", {"start": v(-1.32, -52.07) * mm, "end": v(-1.54, -52.07) * mm});
            skLineSegment(sketch, "E835", {"start": v(-1.54, -52.07) * mm, "end": v(-1.77, -52.07) * mm});
            skLineSegment(sketch, "E836", {"start": v(-1.77, -52.07) * mm, "end": v(-2, -52.07) * mm});
            skLineSegment(sketch, "E837", {"start": v(-2, -52.07) * mm, "end": v(-2.22, -52.07) * mm});
            skLineSegment(sketch, "E838", {"start": v(-2.22, -52.07) * mm, "end": v(-2.44, -52.07) * mm});
            skLineSegment(sketch, "E839", {"start": v(-2.44, -52.07) * mm, "end": v(-2.67, -52.07) * mm});
            skLineSegment(sketch, "E840", {"start": v(-2.67, -52.07) * mm, "end": v(-2.9, -52.07) * mm});
            skLineSegment(sketch, "E841", {"start": v(-2.9, -52.07) * mm, "end": v(-3.12, -52.07) * mm});
            skLineSegment(sketch, "E842", {"start": v(-3.12, -52.07) * mm, "end": v(-3.35, -52.07) * mm});
            skLineSegment(sketch, "E843", {"start": v(-3.35, -52.07) * mm, "end": v(-3.57, -52.07) * mm});
            skLineSegment(sketch, "E844", {"start": v(-3.57, -52.07) * mm, "end": v(-3.8, -52.07) * mm});
            skLineSegment(sketch, "E845", {"start": v(-3.8, -52.07) * mm, "end": v(-4.03, -52.07) * mm});
            skLineSegment(sketch, "E846", {"start": v(-4.03, -52.07) * mm, "end": v(-4.25, -52.07) * mm});
            skLineSegment(sketch, "E847", {"start": v(-4.25, -52.07) * mm, "end": v(-4.48, -52.07) * mm});
            skLineSegment(sketch, "E848", {"start": v(-4.48, -52.07) * mm, "end": v(-4.7, -52.07) * mm});
            skLineSegment(sketch, "E849", {"start": v(-4.7, -52.07) * mm, "end": v(-4.93, -52.07) * mm});
            skLineSegment(sketch, "E850", {"start": v(-4.93, -52.07) * mm, "end": v(-5.15, -52.07) * mm});
            skLineSegment(sketch, "E851", {"start": v(-5.15, -52.07) * mm, "end": v(-5.38, -52.07) * mm});
            skLineSegment(sketch, "E852", {"start": v(-5.38, -52.07) * mm, "end": v(-5.6, -52.07) * mm});
            skLineSegment(sketch, "E853", {"start": v(-5.6, -52.07) * mm, "end": v(-5.83, -52.07) * mm});
            skLineSegment(sketch, "E854", {"start": v(-5.83, -52.07) * mm, "end": v(-6.06, -52.07) * mm});
            skLineSegment(sketch, "E855", {"start": v(-6.06, -52.07) * mm, "end": v(-6.28, -52.07) * mm});
            skLineSegment(sketch, "E856", {"start": v(-6.28, -52.07) * mm, "end": v(-6.5, -52.07) * mm});
            skLineSegment(sketch, "E857", {"start": v(-6.5, -52.07) * mm, "end": v(-6.74, -52.07) * mm});
            skLineSegment(sketch, "E858", {"start": v(-6.74, -52.07) * mm, "end": v(-6.96, -52.07) * mm});
            skLineSegment(sketch, "E859", {"start": v(-6.96, -52.07) * mm, "end": v(-7.19, -52.07) * mm});
            skLineSegment(sketch, "E860", {"start": v(-7.19, -52.07) * mm, "end": v(-7.41, -52.07) * mm});
            skLineSegment(sketch, "E861", {"start": v(-7.41, -52.07) * mm, "end": v(-7.64, -52.07) * mm});
            skLineSegment(sketch, "E862", {"start": v(-7.64, -52.07) * mm, "end": v(-7.86, -52.07) * mm});
            skLineSegment(sketch, "E863", {"start": v(-7.86, -52.07) * mm, "end": v(-8.1, -52.07) * mm});
            skLineSegment(sketch, "E864", {"start": v(-8.1, -52.07) * mm, "end": v(-8.32, -52.07) * mm});
            skLineSegment(sketch, "E865", {"start": v(-8.32, -52.07) * mm, "end": v(-8.54, -52.07) * mm});
            skLineSegment(sketch, "E866", {"start": v(-8.54, -52.07) * mm, "end": v(-8.77, -52.07) * mm});
            skLineSegment(sketch, "E867", {"start": v(-8.77, -52.07) * mm, "end": v(-9, -52.07) * mm});
            skLineSegment(sketch, "E868", {"start": v(-9, -52.07) * mm, "end": v(-9.22, -52.07) * mm});
            skLineSegment(sketch, "E869", {"start": v(-9.22, -52.07) * mm, "end": v(-9.45, -52.07) * mm});
            skLineSegment(sketch, "E870", {"start": v(-9.45, -52.07) * mm, "end": v(-9.67, -52.07) * mm});
            skLineSegment(sketch, "E871", {"start": v(-9.67, -52.07) * mm, "end": v(-9.9, -52.07) * mm});
            skLineSegment(sketch, "E872", {"start": v(-9.9, -52.07) * mm, "end": v(-10.12, -52.07) * mm});
            skLineSegment(sketch, "E873", {"start": v(-10.12, -52.07) * mm, "end": v(-10.35, -52.07) * mm});
            skLineSegment(sketch, "E874", {"start": v(-10.35, -52.07) * mm, "end": v(-10.57, -52.07) * mm});
            skLineSegment(sketch, "E875", {"start": v(-10.57, -52.07) * mm, "end": v(-10.8, -52.07) * mm});
            skLineSegment(sketch, "E876", {"start": v(-10.8, -52.07) * mm, "end": v(-10.8, -50.86) * mm});
            skLineSegment(sketch, "E877", {"start": v(-10.8, -50.86) * mm, "end": v(-10.8, -49.65) * mm});
            skLineSegment(sketch, "E878", {"start": v(-10.8, -49.65) * mm, "end": v(-10.8, -48.44) * mm});
            skLineSegment(sketch, "E879", {"start": v(-10.8, -48.44) * mm, "end": v(-10.8, -47.23) * mm});
            skLineSegment(sketch, "E880", {"start": v(-10.8, -47.23) * mm, "end": v(-10.8, -46.02) * mm});
            skLineSegment(sketch, "E881", {"start": v(-10.8, -46.02) * mm, "end": v(-10.8, -44.81) * mm});
            skLineSegment(sketch, "E882", {"start": v(-10.8, -44.81) * mm, "end": v(-10.8, -43.6) * mm});
            skLineSegment(sketch, "E883", {"start": v(-10.8, -43.6) * mm, "end": v(-10.8, -42.4) * mm});
            skLineSegment(sketch, "E884", {"start": v(-10.8, -42.4) * mm, "end": v(-10.8, -41.19) * mm});
            skLineSegment(sketch, "E885", {"start": v(-10.8, -41.19) * mm, "end": v(-10.8, -39.98) * mm});
            skLineSegment(sketch, "E886", {"start": v(-10.8, -39.98) * mm, "end": v(-10.8, -38.77) * mm});
            skLineSegment(sketch, "E887", {"start": v(-10.8, -38.77) * mm, "end": v(-10.8, -37.56) * mm});
            skLineSegment(sketch, "E888", {"start": v(-10.8, -37.56) * mm, "end": v(-10.8, -36.36) * mm});
            skLineSegment(sketch, "E889", {"start": v(-10.8, -36.36) * mm, "end": v(-10.8, -35.15) * mm});
            skLineSegment(sketch, "E890", {"start": v(-10.8, -35.15) * mm, "end": v(-10.8, -33.94) * mm});
            skLineSegment(sketch, "E891", {"start": v(-10.8, -33.94) * mm, "end": v(-10.8, -32.73) * mm});
            skLineSegment(sketch, "E892", {"start": v(-10.8, -32.73) * mm, "end": v(-10.8, -31.52) * mm});
            skLineSegment(sketch, "E893", {"start": v(-10.8, -31.52) * mm, "end": v(-10.8, -30.31) * mm});
            skLineSegment(sketch, "E894", {"start": v(-10.8, -30.31) * mm, "end": v(-10.8, -29.1) * mm});
            skLineSegment(sketch, "E895", {"start": v(-10.8, -29.1) * mm, "end": v(-10.8, -27.9) * mm});
            skLineSegment(sketch, "E896", {"start": v(-10.8, -27.9) * mm, "end": v(-10.8, -26.69) * mm});
            skLineSegment(sketch, "E897", {"start": v(-10.8, -26.69) * mm, "end": v(-10.8, -25.48) * mm});
            skLineSegment(sketch, "E898", {"start": v(-10.8, -25.48) * mm, "end": v(-10.8, -24.27) * mm});
            skLineSegment(sketch, "E899", {"start": v(-10.8, -24.27) * mm, "end": v(-10.8, -23.06) * mm});
            skLineSegment(sketch, "E900", {"start": v(-10.8, -23.06) * mm, "end": v(-10.8, -21.85) * mm});
            skLineSegment(sketch, "E901", {"start": v(-10.8, -21.85) * mm, "end": v(-10.8, -20.65) * mm});
            skLineSegment(sketch, "E902", {"start": v(-10.8, -20.65) * mm, "end": v(-10.8, -19.44) * mm});
            skLineSegment(sketch, "E903", {"start": v(-10.8, -19.44) * mm, "end": v(-10.8, -18.23) * mm});
            skLineSegment(sketch, "E904", {"start": v(-10.8, -18.23) * mm, "end": v(-10.8, -17.02) * mm});
            skLineSegment(sketch, "E905", {"start": v(-10.8, -17.02) * mm, "end": v(-10.8, -15.81) * mm});
            skLineSegment(sketch, "E906", {"start": v(-10.8, -15.81) * mm, "end": v(-10.8, -14.6) * mm});
            skLineSegment(sketch, "E907", {"start": v(-10.8, -14.6) * mm, "end": v(-10.8, -13.4) * mm});
            skLineSegment(sketch, "E908", {"start": v(-10.8, -13.4) * mm, "end": v(-10.8, -12.19) * mm});
            skLineSegment(sketch, "E909", {"start": v(-10.8, -12.19) * mm, "end": v(-10.8, -10.98) * mm});
            skLineSegment(sketch, "E910", {"start": v(-10.8, -10.98) * mm, "end": v(-10.8, -9.77) * mm});
            skLineSegment(sketch, "E911", {"start": v(-10.8, -9.77) * mm, "end": v(-10.8, -8.56) * mm});
            skLineSegment(sketch, "E912", {"start": v(-10.8, -8.56) * mm, "end": v(-10.8, -7.35) * mm});
            skLineSegment(sketch, "E913", {"start": v(-10.8, -7.35) * mm, "end": v(-10.8, -6.14) * mm});
            skLineSegment(sketch, "E914", {"start": v(-10.8, -6.14) * mm, "end": v(-10.8, -4.94) * mm});
            skLineSegment(sketch, "E915", {"start": v(-10.8, -4.94) * mm, "end": v(-10.8, -3.73) * mm});
            skLineSegment(sketch, "E916", {"start": v(-10.8, -3.73) * mm, "end": v(-10.8, -2.52) * mm});
            skLineSegment(sketch, "E917", {"start": v(-10.8, -2.52) * mm, "end": v(-10.8, -1.3) * mm});
            skLineSegment(sketch, "E918", {"start": v(-10.8, -1.3) * mm, "end": v(-10.8, -0.1) * mm});
            skLineSegment(sketch, "E919", {"start": v(-10.8, -0.1) * mm, "end": v(-10.8, 1.1) * mm});
            skLineSegment(sketch, "E920", {"start": v(-10.8, 1.1) * mm, "end": v(-10.8, 2.32) * mm});
            skLineSegment(sketch, "E921", {"start": v(-10.8, 2.32) * mm, "end": v(-10.8, 3.52) * mm});
            skLineSegment(sketch, "E922", {"start": v(-10.8, 3.52) * mm, "end": v(-10.8, 4.73) * mm});
            skLineSegment(sketch, "E923", {"start": v(-10.8, 4.73) * mm, "end": v(-10.8, 5.94) * mm});
            skLineSegment(sketch, "E924", {"start": v(-10.8, 5.94) * mm, "end": v(-10.8, 7.15) * mm});
            skLineSegment(sketch, "E925", {"start": v(-10.8, 7.15) * mm, "end": v(-10.8, 8.36) * mm});
            skLineSegment(sketch, "E926", {"start": v(-10.8, 8.36) * mm, "end": v(-10.8, 9.57) * mm});
            skLineSegment(sketch, "E927", {"start": v(-10.8, 9.57) * mm, "end": v(-10.8, 10.77) * mm});
            skLineSegment(sketch, "E928", {"start": v(-10.8, 10.77) * mm, "end": v(-10.8, 11.98) * mm});
            skLineSegment(sketch, "E929", {"start": v(-10.8, 11.98) * mm, "end": v(-10.8, 13.2) * mm});
            skLineSegment(sketch, "E930", {"start": v(-10.8, 13.2) * mm, "end": v(-10.8, 14.4) * mm});
            skLineSegment(sketch, "E931", {"start": v(-10.8, 14.4) * mm, "end": v(-10.8, 15.6) * mm});
            skLineSegment(sketch, "E932", {"start": v(-10.8, 15.6) * mm, "end": v(-10.8, 16.82) * mm});
            skLineSegment(sketch, "E933", {"start": v(-10.8, 16.82) * mm, "end": v(-10.8, 18.03) * mm});
            skLineSegment(sketch, "E934", {"start": v(-10.8, 18.03) * mm, "end": v(-10.8, 19.23) * mm});
            skLineSegment(sketch, "E935", {"start": v(-10.8, 19.23) * mm, "end": v(-10.8, 20.44) * mm});
            skLineSegment(sketch, "E936", {"start": v(-10.8, 20.44) * mm, "end": v(-10.8, 21.65) * mm});
            skLineSegment(sketch, "E937", {"start": v(-10.8, 21.65) * mm, "end": v(-10.8, 22.86) * mm});
            skLineSegment(sketch, "E938", {"start": v(-10.8, 22.86) * mm, "end": v(-10.8, 24.07) * mm});
            skLineSegment(sketch, "E939", {"start": v(-10.8, 24.07) * mm, "end": v(-10.8, 25.28) * mm});
            skLineSegment(sketch, "E940", {"start": v(-10.8, 25.28) * mm, "end": v(-10.8, 25.46) * mm});
            skLineSegment(sketch, "E941", {"start": v(-10.8, 25.46) * mm, "end": v(-10.8, 25.64) * mm});
            skLineSegment(sketch, "E942", {"start": v(-10.8, 25.64) * mm, "end": v(-10.8, 25.82) * mm});
            skLineSegment(sketch, "E943", {"start": v(-10.8, 25.82) * mm, "end": v(-10.79, 26) * mm});
            skLineSegment(sketch, "E944", {"start": v(-10.79, 26) * mm, "end": v(-10.78, 26.18) * mm});
            skLineSegment(sketch, "E945", {"start": v(-10.78, 26.18) * mm, "end": v(-10.77, 26.36) * mm});
            skLineSegment(sketch, "E946", {"start": v(-10.77, 26.36) * mm, "end": v(-10.76, 26.54) * mm});
            skLineSegment(sketch, "E947", {"start": v(-10.76, 26.54) * mm, "end": v(-10.75, 26.72) * mm});
            skLineSegment(sketch, "E948", {"start": v(-10.75, 26.72) * mm, "end": v(-10.74, 26.9) * mm});
            skLineSegment(sketch, "E949", {"start": v(-10.74, 26.9) * mm, "end": v(-10.73, 27.08) * mm});
            skLineSegment(sketch, "E950", {"start": v(-10.73, 27.08) * mm, "end": v(-10.71, 27.26) * mm});
            skLineSegment(sketch, "E951", {"start": v(-10.71, 27.26) * mm, "end": v(-10.7, 27.44) * mm});
            skLineSegment(sketch, "E952", {"start": v(-10.7, 27.44) * mm, "end": v(-10.68, 27.62) * mm});
            skLineSegment(sketch, "E953", {"start": v(-10.68, 27.62) * mm, "end": v(-10.66, 27.8) * mm});
            skLineSegment(sketch, "E954", {"start": v(-10.66, 27.8) * mm, "end": v(-10.64, 27.97) * mm});
            skLineSegment(sketch, "E955", {"start": v(-10.64, 27.97) * mm, "end": v(-10.62, 28.15) * mm});
            skLineSegment(sketch, "E956", {"start": v(-10.62, 28.15) * mm, "end": v(-10.6, 28.32) * mm});
            skLineSegment(sketch, "E957", {"start": v(-10.6, 28.32) * mm, "end": v(-10.57, 28.5) * mm});
            skLineSegment(sketch, "E958", {"start": v(-10.57, 28.5) * mm, "end": v(-10.54, 28.68) * mm});
            skLineSegment(sketch, "E959", {"start": v(-10.54, 28.68) * mm, "end": v(-10.51, 28.85) * mm});
            skLineSegment(sketch, "E960", {"start": v(-10.51, 28.85) * mm, "end": v(-10.48, 29.02) * mm});
            skLineSegment(sketch, "E961", {"start": v(-10.48, 29.02) * mm, "end": v(-10.45, 29.2) * mm});
            skLineSegment(sketch, "E962", {"start": v(-10.45, 29.2) * mm, "end": v(-10.42, 29.37) * mm});
            skLineSegment(sketch, "E963", {"start": v(-10.42, 29.37) * mm, "end": v(-10.39, 29.55) * mm});
            skLineSegment(sketch, "E964", {"start": v(-10.39, 29.55) * mm, "end": v(-10.35, 29.72) * mm});
            skLineSegment(sketch, "E965", {"start": v(-10.35, 29.72) * mm, "end": v(-10.32, 29.9) * mm});
            skLineSegment(sketch, "E966", {"start": v(-10.32, 29.9) * mm, "end": v(-10.28, 30.06) * mm});
            skLineSegment(sketch, "E967", {"start": v(-10.28, 30.06) * mm, "end": v(-10.24, 30.23) * mm});
            skLineSegment(sketch, "E968", {"start": v(-10.24, 30.23) * mm, "end": v(-10.2, 30.4) * mm});
            skLineSegment(sketch, "E969", {"start": v(-10.2, 30.4) * mm, "end": v(-10.16, 30.58) * mm});
            skLineSegment(sketch, "E970", {"start": v(-10.16, 30.58) * mm, "end": v(-10.12, 30.75) * mm});
            skLineSegment(sketch, "E971", {"start": v(-10.12, 30.75) * mm, "end": v(-10.08, 30.92) * mm});
            skLineSegment(sketch, "E972", {"start": v(-10.08, 30.92) * mm, "end": v(-10.03, 31.08) * mm});
            skLineSegment(sketch, "E973", {"start": v(-10.03, 31.08) * mm, "end": v(-9.98, 31.25) * mm});
            skLineSegment(sketch, "E974", {"start": v(-9.98, 31.25) * mm, "end": v(-9.94, 31.42) * mm});
            skLineSegment(sketch, "E975", {"start": v(-9.94, 31.42) * mm, "end": v(-9.89, 31.59) * mm});
            skLineSegment(sketch, "E976", {"start": v(-9.89, 31.59) * mm, "end": v(-9.84, 31.76) * mm});
            skLineSegment(sketch, "E977", {"start": v(-9.84, 31.76) * mm, "end": v(-9.79, 31.92) * mm});
            skLineSegment(sketch, "E978", {"start": v(-9.79, 31.92) * mm, "end": v(-9.73, 32.09) * mm});
            skLineSegment(sketch, "E979", {"start": v(-9.73, 32.09) * mm, "end": v(-9.68, 32.25) * mm});
            skLineSegment(sketch, "E980", {"start": v(-9.68, 32.25) * mm, "end": v(-9.62, 32.42) * mm});
            skLineSegment(sketch, "E981", {"start": v(-9.62, 32.42) * mm, "end": v(-9.57, 32.58) * mm});
            skLineSegment(sketch, "E982", {"start": v(-9.57, 32.58) * mm, "end": v(-9.5, 32.75) * mm});
            skLineSegment(sketch, "E983", {"start": v(-9.5, 32.75) * mm, "end": v(-9.45, 32.9) * mm});
            skLineSegment(sketch, "E984", {"start": v(-9.45, 32.9) * mm, "end": v(-9.4, 33.07) * mm});
            skLineSegment(sketch, "E985", {"start": v(-9.4, 33.07) * mm, "end": v(-9.33, 33.23) * mm});
            skLineSegment(sketch, "E986", {"start": v(-9.33, 33.23) * mm, "end": v(-9.27, 33.4) * mm});
            skLineSegment(sketch, "E987", {"start": v(-9.27, 33.4) * mm, "end": v(-9.2, 33.56) * mm});
            skLineSegment(sketch, "E988", {"start": v(-9.2, 33.56) * mm, "end": v(-9.14, 33.72) * mm});
            skLineSegment(sketch, "E989", {"start": v(-9.14, 33.72) * mm, "end": v(-9.07, 33.88) * mm});
            skLineSegment(sketch, "E990", {"start": v(-9.07, 33.88) * mm, "end": v(-9, 34.04) * mm});
            skLineSegment(sketch, "E991", {"start": v(-9, 34.04) * mm, "end": v(-8.93, 34.2) * mm});
            skLineSegment(sketch, "E992", {"start": v(-8.93, 34.2) * mm, "end": v(-8.86, 34.35) * mm});
            skLineSegment(sketch, "E993", {"start": v(-8.86, 34.35) * mm, "end": v(-8.8, 34.5) * mm});
            skLineSegment(sketch, "E994", {"start": v(-8.8, 34.5) * mm, "end": v(-8.72, 34.67) * mm});
            skLineSegment(sketch, "E995", {"start": v(-8.72, 34.67) * mm, "end": v(-8.65, 34.82) * mm});
            skLineSegment(sketch, "E996", {"start": v(-8.65, 34.82) * mm, "end": v(-8.57, 34.98) * mm});
            skLineSegment(sketch, "E997", {"start": v(-8.57, 34.98) * mm, "end": v(-8.5, 35.13) * mm});
            skLineSegment(sketch, "E998", {"start": v(-8.5, 35.13) * mm, "end": v(-8.42, 35.29) * mm});
            skLineSegment(sketch, "E999", {"start": v(-8.42, 35.29) * mm, "end": v(-8.34, 35.44) * mm});
            skLineSegment(sketch, "E1000", {"start": v(-8.34, 35.44) * mm, "end": v(-8.26, 35.6) * mm});
            skLineSegment(sketch, "E1001", {"start": v(-8.26, 35.6) * mm, "end": v(-8.18, 35.74) * mm});
            skLineSegment(sketch, "E1002", {"start": v(-8.18, 35.74) * mm, "end": v(-8.1, 35.9) * mm});
            skLineSegment(sketch, "E1003", {"start": v(-8.1, 35.9) * mm, "end": v(-8.02, 36.05) * mm});
            skLineSegment(sketch, "E1004", {"start": v(-8.02, 36.05) * mm, "end": v(-7.8, 36.33) * mm});
            skLineSegment(sketch, "E1005", {"start": v(-7.8, 36.33) * mm, "end": v(-7.6, 36.62) * mm});
            skLineSegment(sketch, "E1006", {"start": v(-7.6, 36.62) * mm, "end": v(-7.38, 36.9) * mm});
            skLineSegment(sketch, "E1007", {"start": v(-7.38, 36.9) * mm, "end": v(-7.16, 37.18) * mm});
            skLineSegment(sketch, "E1008", {"start": v(-7.16, 37.18) * mm, "end": v(-6.93, 37.45) * mm});
            skLineSegment(sketch, "E1009", {"start": v(-6.93, 37.45) * mm, "end": v(-6.7, 37.73) * mm});
            skLineSegment(sketch, "E1010", {"start": v(-6.7, 37.73) * mm, "end": v(-6.47, 38) * mm});
            skLineSegment(sketch, "E1011", {"start": v(-6.47, 38) * mm, "end": v(-6.24, 38.26) * mm});
            skLineSegment(sketch, "E1012", {"start": v(-6.24, 38.26) * mm, "end": v(-6, 38.52) * mm});
            skLineSegment(sketch, "E1013", {"start": v(-6, 38.52) * mm, "end": v(-5.76, 38.78) * mm});
            skLineSegment(sketch, "E1014", {"start": v(-5.76, 38.78) * mm, "end": v(-5.51, 39.03) * mm});
            skLineSegment(sketch, "E1015", {"start": v(-5.51, 39.03) * mm, "end": v(-5.26, 39.28) * mm});
            skLineSegment(sketch, "E1016", {"start": v(-5.26, 39.28) * mm, "end": v(-5.01, 39.53) * mm});
            skLineSegment(sketch, "E1017", {"start": v(-5.01, 39.53) * mm, "end": v(-4.76, 39.77) * mm});
            skLineSegment(sketch, "E1018", {"start": v(-4.76, 39.77) * mm, "end": v(-4.5, 40.01) * mm});
            skLineSegment(sketch, "E1019", {"start": v(-4.5, 40.01) * mm, "end": v(-4.23, 40.25) * mm});
            skLineSegment(sketch, "E1020", {"start": v(-4.23, 40.25) * mm, "end": v(-3.97, 40.48) * mm});
            skLineSegment(sketch, "E1021", {"start": v(-3.97, 40.48) * mm, "end": v(-3.7, 40.7) * mm});
            skLineSegment(sketch, "E1022", {"start": v(-3.7, 40.7) * mm, "end": v(-3.43, 40.93) * mm});
            skLineSegment(sketch, "E1023", {"start": v(-3.43, 40.93) * mm, "end": v(-3.15, 41.15) * mm});
            skLineSegment(sketch, "E1024", {"start": v(-3.15, 41.15) * mm, "end": v(-2.87, 41.37) * mm});
            skLineSegment(sketch, "E1025", {"start": v(-2.87, 41.37) * mm, "end": v(-2.6, 41.58) * mm});
            skLineSegment(sketch, "E1026", {"start": v(-2.6, 41.58) * mm, "end": v(-2.31, 41.79) * mm});
            skLineSegment(sketch, "E1027", {"start": v(-2.31, 41.79) * mm, "end": v(-2.02, 41.99) * mm});
            skLineSegment(sketch, "E1028", {"start": v(-2.02, 41.99) * mm, "end": v(-1.73, 42.19) * mm});
            skLineSegment(sketch, "E1029", {"start": v(-1.73, 42.19) * mm, "end": v(-1.44, 42.38) * mm});
            skLineSegment(sketch, "E1030", {"start": v(-1.44, 42.38) * mm, "end": v(-1.15, 42.57) * mm});
            skLineSegment(sketch, "E1031", {"start": v(-1.15, 42.57) * mm, "end": v(-0.85, 42.76) * mm});
            skLineSegment(sketch, "E1032", {"start": v(-0.85, 42.76) * mm, "end": v(-0.55, 42.94) * mm});
            skLineSegment(sketch, "E1033", {"start": v(-0.55, 42.94) * mm, "end": v(-0.24, 43.12) * mm});
            skLineSegment(sketch, "E1034", {"start": v(-0.24, 43.12) * mm, "end": v(0.06, 43.3) * mm});
            skLineSegment(sketch, "E1035", {"start": v(0.06, 43.3) * mm, "end": v(0.37, 43.46) * mm});
            skLineSegment(sketch, "E1036", {"start": v(0.37, 43.46) * mm, "end": v(0.68, 43.62) * mm});
            skLineSegment(sketch, "E1037", {"start": v(0.68, 43.62) * mm, "end": v(1, 43.78) * mm});
            skLineSegment(sketch, "E1038", {"start": v(1, 43.78) * mm, "end": v(1.31, 43.94) * mm});
            skLineSegment(sketch, "E1039", {"start": v(1.31, 43.94) * mm, "end": v(1.63, 44.09) * mm});
            skLineSegment(sketch, "E1040", {"start": v(1.63, 44.09) * mm, "end": v(1.95, 44.23) * mm});
            skLineSegment(sketch, "E1041", {"start": v(1.95, 44.23) * mm, "end": v(2.28, 44.38) * mm});
            skLineSegment(sketch, "E1042", {"start": v(2.28, 44.38) * mm, "end": v(2.6, 44.51) * mm});
            skLineSegment(sketch, "E1043", {"start": v(2.6, 44.51) * mm, "end": v(2.93, 44.64) * mm});
            skLineSegment(sketch, "E1044", {"start": v(2.93, 44.64) * mm, "end": v(3.26, 44.77) * mm});
            skLineSegment(sketch, "E1045", {"start": v(3.26, 44.77) * mm, "end": v(3.6, 44.9) * mm});
            skLineSegment(sketch, "E1046", {"start": v(3.6, 44.9) * mm, "end": v(3.93, 45) * mm});
            skLineSegment(sketch, "E1047", {"start": v(3.93, 45) * mm, "end": v(4.27, 45.12) * mm});
            skLineSegment(sketch, "E1048", {"start": v(4.27, 45.12) * mm, "end": v(4.6, 45.22) * mm});
            skLineSegment(sketch, "E1049", {"start": v(4.6, 45.22) * mm, "end": v(4.95, 45.33) * mm});
            skLineSegment(sketch, "E1050", {"start": v(4.95, 45.33) * mm, "end": v(5.3, 45.42) * mm});
            skLineSegment(sketch, "E1051", {"start": v(5.3, 45.42) * mm, "end": v(5.64, 45.51) * mm});
            skLineSegment(sketch, "E1052", {"start": v(5.64, 45.51) * mm, "end": v(5.99, 45.6) * mm});
            skLineSegment(sketch, "E1053", {"start": v(5.99, 45.6) * mm, "end": v(6.33, 45.68) * mm});
            skLineSegment(sketch, "E1054", {"start": v(6.33, 45.68) * mm, "end": v(6.69, 45.76) * mm});
            skLineSegment(sketch, "E1055", {"start": v(6.69, 45.76) * mm, "end": v(7.04, 45.83) * mm});
            skLineSegment(sketch, "E1056", {"start": v(7.04, 45.83) * mm, "end": v(7.4, 45.89) * mm});
            skLineSegment(sketch, "E1057", {"start": v(7.4, 45.89) * mm, "end": v(7.75, 45.95) * mm});
            skLineSegment(sketch, "E1058", {"start": v(7.75, 45.95) * mm, "end": v(8.1, 46) * mm});
            skLineSegment(sketch, "E1059", {"start": v(8.1, 46) * mm, "end": v(8.47, 46.05) * mm});
            skLineSegment(sketch, "E1060", {"start": v(8.47, 46.05) * mm, "end": v(8.83, 46.1) * mm});
            skLineSegment(sketch, "E1061", {"start": v(8.83, 46.1) * mm, "end": v(9.2, 46.13) * mm});
            skLineSegment(sketch, "E1062", {"start": v(9.2, 46.13) * mm, "end": v(9.56, 46.16) * mm});
            skLineSegment(sketch, "E1063", {"start": v(9.56, 46.16) * mm, "end": v(9.92, 46.19) * mm});
            skLineSegment(sketch, "E1064", {"start": v(9.92, 46.19) * mm, "end": v(10.29, 46.2) * mm});
            skLineSegment(sketch, "E1065", {"start": v(10.29, 46.2) * mm, "end": v(10.66, 46.22) * mm});
            skLineSegment(sketch, "E1066", {"start": v(10.66, 46.22) * mm, "end": v(11.03, 46.23) * mm});
            skLineSegment(sketch, "E1067", {"start": v(11.03, 46.23) * mm, "end": v(11.4, 46.24) * mm});
            skLineSegment(sketch, "E1068", {"start": v(11.4, 46.24) * mm, "end": v(11.4, 46.34) * mm});
            skLineSegment(sketch, "E1069", {"start": v(11.4, 46.34) * mm, "end": v(11.4, 46.44) * mm});
            skLineSegment(sketch, "E1070", {"start": v(11.4, 46.44) * mm, "end": v(11.4, 46.54) * mm});
            skLineSegment(sketch, "E1071", {"start": v(11.4, 46.54) * mm, "end": v(11.4, 46.64) * mm});
            skLineSegment(sketch, "E1072", {"start": v(11.4, 46.64) * mm, "end": v(11.4, 46.74) * mm});
            skLineSegment(sketch, "E1073", {"start": v(11.4, 46.74) * mm, "end": v(11.4, 46.84) * mm});
            skLineSegment(sketch, "E1074", {"start": v(11.4, 46.84) * mm, "end": v(11.4, 46.94) * mm});
            skLineSegment(sketch, "E1075", {"start": v(11.4, 46.94) * mm, "end": v(11.4, 47.04) * mm});
            skLineSegment(sketch, "E1076", {"start": v(11.4, 47.04) * mm, "end": v(11.4, 47.14) * mm});
            skLineSegment(sketch, "E1077", {"start": v(11.4, 47.14) * mm, "end": v(11.4, 47.24) * mm});
            skLineSegment(sketch, "E1078", {"start": v(11.4, 47.24) * mm, "end": v(11.4, 47.34) * mm});
            skLineSegment(sketch, "E1079", {"start": v(11.4, 47.34) * mm, "end": v(11.4, 47.44) * mm});
            skLineSegment(sketch, "E1080", {"start": v(11.4, 47.44) * mm, "end": v(11.4, 47.54) * mm});
            skLineSegment(sketch, "E1081", {"start": v(11.4, 47.54) * mm, "end": v(11.4, 47.64) * mm});
            skLineSegment(sketch, "E1082", {"start": v(11.4, 47.64) * mm, "end": v(11.4, 47.74) * mm});
            skLineSegment(sketch, "E1083", {"start": v(11.4, 47.74) * mm, "end": v(11.4, 47.84) * mm});
            skLineSegment(sketch, "E1084", {"start": v(11.4, 47.84) * mm, "end": v(11.4, 47.94) * mm});
            skLineSegment(sketch, "E1085", {"start": v(11.4, 47.94) * mm, "end": v(11.4, 48.04) * mm});
            skLineSegment(sketch, "E1086", {"start": v(11.4, 48.04) * mm, "end": v(11.4, 48.14) * mm});
            skLineSegment(sketch, "E1087", {"start": v(11.4, 48.14) * mm, "end": v(11.4, 48.24) * mm});
            skLineSegment(sketch, "E1088", {"start": v(11.4, 48.24) * mm, "end": v(11.4, 48.35) * mm});
            skLineSegment(sketch, "E1089", {"start": v(11.4, 48.35) * mm, "end": v(11.4, 48.45) * mm});
            skLineSegment(sketch, "E1090", {"start": v(11.4, 48.45) * mm, "end": v(11.4, 48.55) * mm});
            skLineSegment(sketch, "E1091", {"start": v(11.4, 48.55) * mm, "end": v(11.4, 48.65) * mm});
            skLineSegment(sketch, "E1092", {"start": v(11.4, 48.65) * mm, "end": v(11.4, 48.75) * mm});
            skLineSegment(sketch, "E1093", {"start": v(11.4, 48.75) * mm, "end": v(11.4, 48.85) * mm});
            skLineSegment(sketch, "E1094", {"start": v(11.4, 48.85) * mm, "end": v(11.4, 48.95) * mm});
            skLineSegment(sketch, "E1095", {"start": v(11.4, 48.95) * mm, "end": v(11.4, 49.05) * mm});
            skLineSegment(sketch, "E1096", {"start": v(11.4, 49.05) * mm, "end": v(11.4, 49.15) * mm});
            skLineSegment(sketch, "E1097", {"start": v(11.4, 49.15) * mm, "end": v(11.4, 49.25) * mm});
            skLineSegment(sketch, "E1098", {"start": v(11.4, 49.25) * mm, "end": v(11.4, 49.35) * mm});
            skLineSegment(sketch, "E1099", {"start": v(11.4, 49.35) * mm, "end": v(11.4, 49.45) * mm});
            skLineSegment(sketch, "E1100", {"start": v(11.4, 49.45) * mm, "end": v(11.4, 49.55) * mm});
            skLineSegment(sketch, "E1101", {"start": v(11.4, 49.55) * mm, "end": v(11.4, 49.65) * mm});
            skLineSegment(sketch, "E1102", {"start": v(11.4, 49.65) * mm, "end": v(11.4, 49.75) * mm});
            skLineSegment(sketch, "E1103", {"start": v(11.4, 49.75) * mm, "end": v(11.4, 49.85) * mm});
            skLineSegment(sketch, "E1104", {"start": v(11.4, 49.85) * mm, "end": v(11.4, 49.95) * mm});
            skLineSegment(sketch, "E1105", {"start": v(11.4, 49.95) * mm, "end": v(11.4, 50.05) * mm});
            skLineSegment(sketch, "E1106", {"start": v(11.4, 50.05) * mm, "end": v(11.4, 50.15) * mm});
            skLineSegment(sketch, "E1107", {"start": v(11.4, 50.15) * mm, "end": v(11.4, 50.25) * mm});
            skLineSegment(sketch, "E1108", {"start": v(11.4, 50.25) * mm, "end": v(11.4, 50.35) * mm});
            skLineSegment(sketch, "E1109", {"start": v(11.4, 50.35) * mm, "end": v(11.4, 50.46) * mm});
            skLineSegment(sketch, "E1110", {"start": v(11.4, 50.46) * mm, "end": v(11.4, 50.56) * mm});
            skLineSegment(sketch, "E1111", {"start": v(11.4, 50.56) * mm, "end": v(11.4, 50.66) * mm});
            skLineSegment(sketch, "E1112", {"start": v(11.4, 50.66) * mm, "end": v(11.4, 50.76) * mm});
            skLineSegment(sketch, "E1113", {"start": v(11.4, 50.76) * mm, "end": v(11.4, 50.86) * mm});
            skLineSegment(sketch, "E1114", {"start": v(11.4, 50.86) * mm, "end": v(11.4, 50.96) * mm});
            skLineSegment(sketch, "E1115", {"start": v(11.4, 50.96) * mm, "end": v(11.4, 51.06) * mm});
            skLineSegment(sketch, "E1116", {"start": v(11.4, 51.06) * mm, "end": v(11.4, 51.16) * mm});
            skLineSegment(sketch, "E1117", {"start": v(11.4, 51.16) * mm, "end": v(11.4, 51.26) * mm});
            skLineSegment(sketch, "E1118", {"start": v(11.4, 51.26) * mm, "end": v(11.4, 51.36) * mm});
            skLineSegment(sketch, "E1119", {"start": v(11.4, 51.36) * mm, "end": v(11.4, 51.46) * mm});
            skLineSegment(sketch, "E1120", {"start": v(11.4, 51.46) * mm, "end": v(11.4, 51.56) * mm});
            skLineSegment(sketch, "E1121", {"start": v(11.4, 51.56) * mm, "end": v(11.4, 51.66) * mm});
            skLineSegment(sketch, "E1122", {"start": v(11.4, 51.66) * mm, "end": v(11.4, 51.76) * mm});
            skLineSegment(sketch, "E1123", {"start": v(11.4, 51.76) * mm, "end": v(11.4, 51.86) * mm});
            skLineSegment(sketch, "E1124", {"start": v(11.4, 51.86) * mm, "end": v(11.4, 51.96) * mm});
            skLineSegment(sketch, "E1125", {"start": v(11.4, 51.96) * mm, "end": v(11.4, 52.06) * mm});
            skLineSegment(sketch, "E1126", {"start": v(11.4, 52.06) * mm, "end": v(11.4, 52.16) * mm});
            skLineSegment(sketch, "E1127", {"start": v(11.4, 52.16) * mm, "end": v(11.4, 52.26) * mm});
            skLineSegment(sketch, "E1128", {"start": v(11.4, 52.26) * mm, "end": v(11.4, 52.36) * mm});
            skLineSegment(sketch, "E1129", {"start": v(11.4, 52.36) * mm, "end": v(11.4, 52.46) * mm});
            skLineSegment(sketch, "E1130", {"start": v(11.4, 52.46) * mm, "end": v(11.4, 52.57) * mm});
            skLineSegment(sketch, "E1131", {"start": v(11.4, 52.57) * mm, "end": v(11.4, 52.67) * mm});
            skLineSegment(sketch, "E1132", {"start": v(11.4, 52.67) * mm, "end": v(11.35, 52.66) * mm});
            skSolve(sketch);
        }
        {
            var Q0;
            Q0 = qSketchRegion(id + "F0", true);
            var Q1;
            Q1=sQuery(id+"F0.wireOp",EDGE,"E1094");
            revolve(context, id + "F1", {"entities" : qUnion([Q0]), "axis" : qUnion([Q1]), "revolveType" : RevolveType.FULL});
        }
    });
